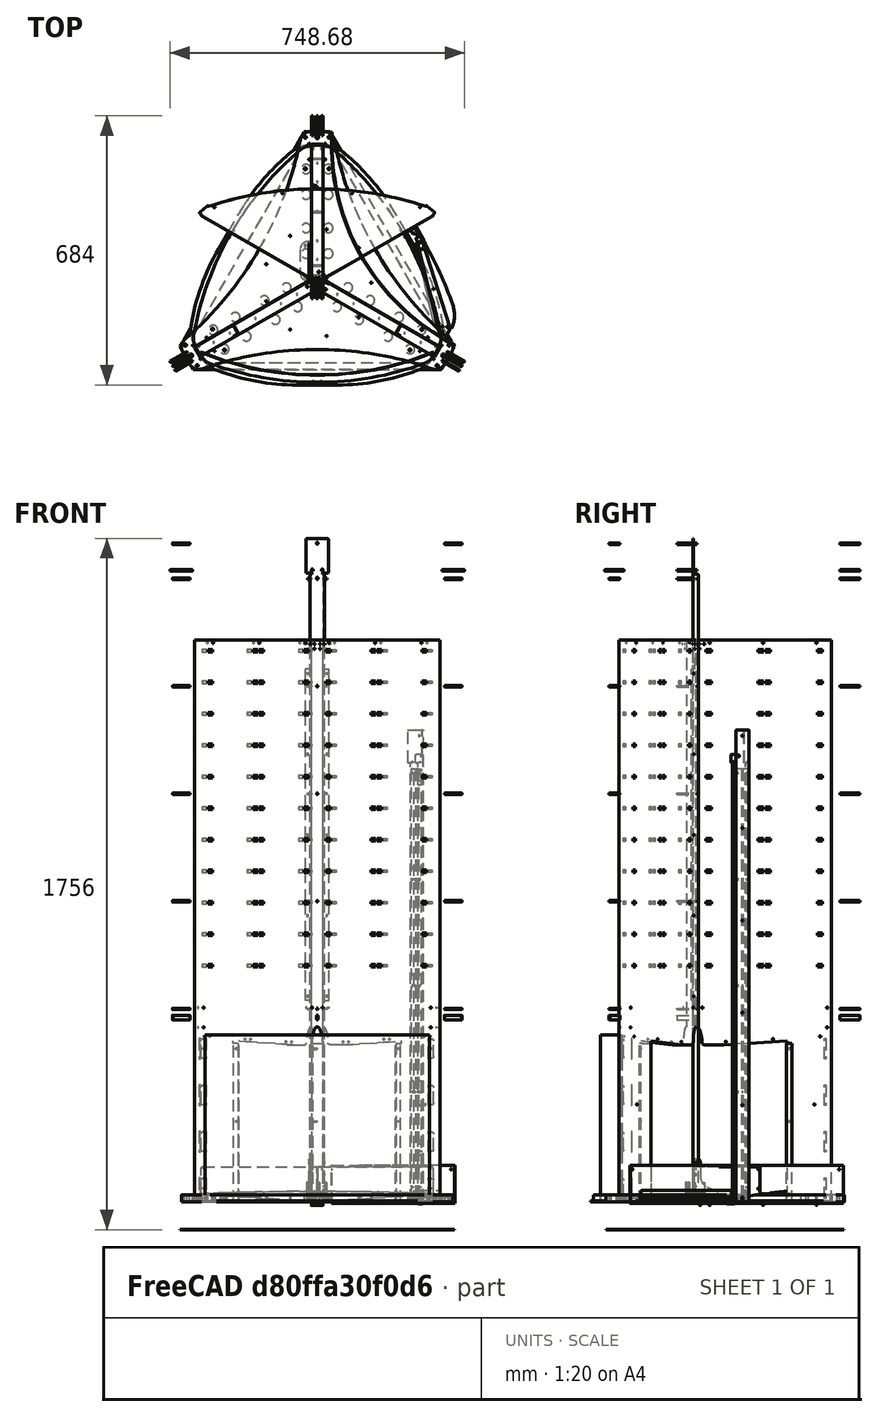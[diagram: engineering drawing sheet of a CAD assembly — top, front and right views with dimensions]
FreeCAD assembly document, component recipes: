
FREECAD ASSEMBLY — COMPONENT RECIPES ("composit_full_size3_door")

This assembly document has 79 components, labeled P0..P78 below (a component is one placed body or linked part). 75 of them carry a construction recipe — the FreeCAD feature program that regenerates the part from scratch, quoted from this document or its linked companion documents; the rest are supplied as boundary geometry only. No exploded tour is included for this assembly.
NOTE — this tour is split across 3 documents so each fits a 32k-token context. This is document 1: the component sections continue in the remaining 2 documents, each repeating the header above.
COMPONENT P0 — recipe-attached ("tech_sector_pillar_material_0.30ansi", modeled in this document).
Construction recipe (the document's own serialized feature program — sketch geometry with constraints, then the solid features built on it; lengths are millimeters unless a unit is written):

FEATURE [Sketcher::SketchObject] Sketch062
  AttachmentSupport = -> [XY_Plane036]
  FullyConstrained = true
  MapMode = 5
  expr: Constraints[3] = <<Properties>>.endface_width / 2 + 0.5 mm
  sketch-geometry (7):
    g0: LineSegment StartX=61.9452 StartY=297.209 StartZ=0 EndX=15 EndY=280 EndZ=0
    g1: LineSegment StartX=15 StartY=280 StartZ=0 EndX=15 EndY=335 EndZ=0
    g2: LineSegment StartX=15 StartY=335 StartZ=0 EndX=62.031 EndY=297.743 EndZ=0
    g3: LineSegment StartX=61.9452 StartY=297.209 StartZ=0 EndX=62.4647 EndY=297.399 EndZ=0
    g4: LineSegment StartX=62.4647 StartY=297.399 StartZ=0 EndX=62.031 EndY=297.743 EndZ=0
    g5: LineSegment StartX=61.9452 StartY=297.209 StartZ=0 EndX=61.8385 EndY=297.5 EndZ=0
    g6: LineSegment StartX=61.8385 StartY=297.5 StartZ=0 EndX=62.031 EndY=297.743 EndZ=0
  constraints (20):
    c: Coincident(g0,g1)
    c: Vertical(g1)
    c: Coincident(g1,g2)
    c: DistanceX(g1) = 15
    c: Distance(g1) = 55
    c: Distance(g2) = 60
    c: Distance(g0) = 50
    c: Coincident(g3,g0)
    c: Coincident(g4,g3)
    c: Coincident(g4,g2)
    c: Parallel(g0,g3)
    c: Parallel(g4,g2)
    c: Equal(g3,g4)
    c: Coincident(g0,g5)
    c: Coincident(g5,g6)
    c: Coincident(g6,g2)
    c: Perpendicular(g3,g5)
    c: Perpendicular(g4,g6)
    c: Distance(g5) = 0.31
    c: DistanceY(g1) = 335
FEATURE [PartDesign::FeaturePython] BaseBend020  # WARN: FeaturePython — macro-defined, semantics opaque (R4)
  BendSide = 0
  BendSketch = -> Sketch062
  MidPlane = false
  Reverse = false
  Suppressed = false
  length = 413
  radius = 0.1
  thickness = 0.3
  expr: radius = composit_properties#<<Properties>>.bend_r
  expr: thickness = composit_properties#<<Properties>>.al_thickness
FEATURE [PartDesign::FeaturePython] Bend009  # WARN: FeaturePython — macro-defined, semantics opaque (R4)
  AutoMiter = true
  BaseFeature = -> BaseBend020
  BendType = 0
  LengthList = [15]
  LengthSpec = 0
  ReliefFactor = 0.7
  Suppressed = false
  UseReliefFactor = false
  angle = 90
  baseObject = -> BaseBend020 [Edge17,Edge4,Edge33,Edge32,Edge16,Edge3]
  bendAList = [90]
  extend1 = 0
  extend2 = 0
  gap1 = 0
  gap2 = 0
  invert = false
  kfactor = 0.5
  length = 15
  maxExtendDist = 5
  minGap = 0.1
  minReliefGap = 1
  miterangle1 = 0
  miterangle2 = 0
  offset = 0
  radius = 0.1
  reliefType = 0
  reliefd = 1
  reliefw = 0.8
  sketchflip = false
  sketchinvert = false
  unfold = false
  expr: radius = BaseBend020.radius
FEATURE [Sketcher::SketchObject] Sketch075
  AttachmentSupport = -> [XY_Plane036]
  ExternalGeometry = -> [Sketch062]
  FullyConstrained = true
  MapMode = 5
  expr: Constraints[34] = <<Properties>>.rivet_d
  sketch-geometry (14):
    g0: LineSegment StartX=15 StartY=280 StartZ=0 EndX=62.4647 EndY=297.399 EndZ=0
    g1: LineSegment StartX=62.4647 StartY=297.399 StartZ=0 EndX=15 EndY=335 EndZ=0
    g2: LineSegment StartX=15 StartY=280 StartZ=0 EndX=30.7162 EndY=302.5 EndZ=0
    g3: LineSegment StartX=30.7162 StartY=302.5 StartZ=0 EndX=15 EndY=335 EndZ=0
    g4: LineSegment StartX=30.7162 StartY=302.5 StartZ=0 EndX=62.4647 EndY=297.399 EndZ=0
    g5: LineSegment StartX=15 StartY=302.5 StartZ=0 EndX=30.7162 EndY=302.5 EndZ=0
    g6: LineSegment StartX=30.7162 StartY=302.5 StartZ=0 EndX=36.1253 EndY=287.744 EndZ=0
    g7: LineSegment StartX=30.7162 StartY=302.5 StartZ=0 EndX=40.4751 EndY=314.819 EndZ=0
    g8: Circle CenterX=34.4044 CenterY=292.439 CenterZ=0 NormalX=0 NormalY=0 NormalZ=1 AngleXU=0 Radius=1.7
    g9: Circle CenterX=36.2097 CenterY=309.435 CenterZ=0 NormalX=0 NormalY=0 NormalZ=1 AngleXU=0 Radius=1.7
    g10: Circle CenterX=20.588 CenterY=302.5 CenterZ=0 NormalX=0 NormalY=0 NormalZ=1 AngleXU=0 Radius=1.7
    g11: LineSegment StartX=20.588 StartY=302.5 StartZ=0 EndX=36.2097 EndY=309.435 EndZ=0
    g12: LineSegment StartX=36.2097 StartY=309.435 StartZ=0 EndX=34.4044 EndY=292.439 EndZ=0
    g13: LineSegment StartX=34.4044 StartY=292.439 StartZ=0 EndX=20.588 EndY=302.5 EndZ=0
  constraints (36):
    c: Coincident(g-4,g0)
    c: Coincident(g0,g1)
    c: Coincident(g1,g-3)
    c: PointOnObject(g-4,g0)
    c: PointOnObject(g-3,g1)
    c: Coincident(g0,g2)
    c: Coincident(g2,g3)
    c: Coincident(g2,g4)
    c: Coincident(g4,g0)
    c: Coincident(g3,g1)
    c: Coincident(g5,g2)
    c: Horizontal(g5)
    c: Coincident(g5,g6)
    c: PointOnObject(g6,g0)
    c: Perpendicular(g0,g6)
    c: Vertical(g5,g0)
    c: Equal(g6,g5)
    c: Coincident(g7,g2)
    c: PointOnObject(g7,g1)
    c: Perpendicular(g1,g7)
    c: Equal(g6,g7)
    c: PointOnObject(g8,g6)
    c: PointOnObject(g9,g7)
    c: PointOnObject(g10,g5)
    c: Coincident(g11,g10)
    c: Coincident(g11,g9)
    c: Coincident(g11,g12)
    c: Coincident(g12,g8)
    c: Coincident(g12,g13)
    c: Coincident(g13,g11)
    c: Equal(g13,g11)
    c: Equal(g11,g12)
    c: Equal(g8,g10)
    c: Equal(g8,g9)
    c: Diameter(g8) = 3.4
    c: Distance(g8,g6) = 5
FEATURE [PartDesign::Pocket] Pocket035
  BaseFeature = -> Bend009
  Direction = (0,0,-1)
  Length = 5
  Length2 = 5
  Midplane = true
  Profile = -> Sketch075
  ReferenceAxis = -> Sketch075 [N_Axis]
  Suppressed = false
  Type = 1
FEATURE [PartDesign::Plane] DatumPlane001
  AttachmentOffset = pos=(0,0,0) rot=(0,1,0;1.5708rad)
  AttachmentSupport = -> [Sketch062]
  Length = 411.982
  MapMode = 7
  Placement = pos=(15,335,0) rot=(-0.89718,0.312304,0.312304;4.6041rad)
  ResizeMode = 0
  Width = 515.08
FEATURE [Sketcher::SketchObject] Sketch077
  AttachmentSupport = -> [DatumPlane001]
  FullyConstrained = true
  MapMode = 5
  Placement = pos=(15,335,0) rot=(0.89718,-0.312304,-0.312304;1.67908rad)
  expr: Constraints[1] = <<Properties>>.rivet_d
  expr: Constraints[3] = BaseBend020.length
  sketch-geometry (4):
    g0: Circle CenterX=10 CenterY=7 CenterZ=0 NormalX=0 NormalY=0 NormalZ=1 AngleXU=0 Radius=1.7
    g1: Circle CenterX=10 CenterY=406 CenterZ=0 NormalX=0 NormalY=0 NormalZ=1 AngleXU=0 Radius=1.7
    g2: GeomPoint X=0 Y=413 Z=0
    g3: LineSegment StartX=0 StartY=206.5 StartZ=0 EndX=10 EndY=206.5 EndZ=0
  constraints (10):
    c: Equal(g0,g1)
    c: Diameter(g0) = 3.4
    c: PointOnObject(g2,g-2)
    c: DistanceY(g2) = 413
    c: DistanceX(g0) = 10
    c: DistanceY(g0) = 7
    c: Vertical(g1,g0)
    c: Horizontal(g3)
    c: Symmetric(g-1,g2,g3)
    c: Symmetric(g1,g0,g3)
FEATURE [PartDesign::Hole] Hole006
  BaseFeature = -> Pocket035
  CustomThreadClearance = 0
  Depth = 1
  DepthType = 0
  Diameter = 3.4
  DrillForDepth = false
  DrillPoint = 1
  DrillPointAngle = 118
  HoleCutCountersinkAngle = 90
  HoleCutCustomValues = false
  HoleCutDepth = 0
  HoleCutDiameter = 6.1
  HoleCutType = 0
  ModelThread = false
  Profile = -> Sketch077
  Reversed = true
  Suppressed = false
  Tapered = false
  TaperedAngle = 90
  ThreadClass = 0
  ThreadDepth = 1
  ThreadDepthType = 0
  ThreadDirection = 0
  ThreadFit = 0
  ThreadSize = 0
  ThreadType = 0
  Threaded = false
  UseCustomThreadClearance = false
  expr: Diameter = <<Properties>>.rivet_d
FEATURE [Sketcher::SketchObject] Sketch078  label="pillar_magnet_fix"
  AttachmentOffset = pos=(0,0,0) rot=(0,1,0;1.5708rad)
  AttachmentSupport = -> [Sketch062]
  FullyConstrained = true
  MapMode = 7
  Placement = pos=(15,280,0) rot=(0.57735,0.57735,0.57735;2.0944rad)
  expr: Constraints[11] = <<Properties>>.rivet_d
  sketch-geometry (8):
    g0: ArcOfCircle CenterX=32.5 CenterY=244.5 CenterZ=0 NormalX=0 NormalY=0 NormalZ=1 AngleXU=0 Radius=11 StartAngle=4.71239 EndAngle=7.85398
    g1: ArcOfCircle CenterX=27.5 CenterY=244.5 CenterZ=0 NormalX=0 NormalY=0 NormalZ=1 AngleXU=0 Radius=11 StartAngle=1.5708 EndAngle=4.71239
    g2: LineSegment StartX=32.5 StartY=255.5 StartZ=0 EndX=27.5 EndY=255.5 EndZ=0
    g3: LineSegment StartX=27.5 StartY=233.5 StartZ=0 EndX=32.5 EndY=233.5 EndZ=0
    g4: Circle CenterX=30 CenterY=224.5 CenterZ=0 NormalX=0 NormalY=0 NormalZ=1 AngleXU=0 Radius=1.7
    g5: Circle CenterX=30 CenterY=264.5 CenterZ=0 NormalX=0 NormalY=0 NormalZ=1 AngleXU=0 Radius=1.7
    g6: LineSegment StartX=27.5 StartY=244.5 StartZ=0 EndX=30 EndY=244.5 EndZ=0
    g7: LineSegment StartX=32.5 StartY=244.5 StartZ=0 EndX=30 EndY=244.5 EndZ=0
  constraints (20):
    c: Tangent(g0,g2) = -1.5708
    c: Tangent(g2,g1) = -1.5708
    c: Tangent(g1,g3) = -1.5708
    c: Tangent(g3,g0) = -1.5708
    c: Equal(g0,g1)
    c: Coincident(g6,g1)
    c: Coincident(g7,g0)
    c: Coincident(g7,g6)
    c: Equal(g6,g7)
    c: Symmetric(g4,g5,g6)
    c: Equal(g4,g5)
    c: Diameter(g4) = 3.4
    c: Parallel(g6,g7)
    c: Distance(g1,g0) = 5
    c: Diameter(g0) = 22
    c: Horizontal(g1,g0)
    c: DistanceY(g4,g5) = 40
    c: DistanceY(g6) = 244.5  'height'
    c: DistanceX(g6) = 30
    c: Vertical(g4,g5)
FEATURE [PartDesign::Pocket] Pocket037
  BaseFeature = -> Hole006
  Direction = (-1,2e-16,0)
  Length = 5
  Length2 = 5
  Midplane = true
  Profile = -> Sketch078
  ReferenceAxis = -> Sketch078 [N_Axis]
  Suppressed = false
  Type = 0
FEATURE [Sketcher::SketchObject] Sketch079
  AttachmentSupport = -> [DatumPlane001]
  FullyConstrained = true
  MapMode = 5
  Placement = pos=(15,335,0) rot=(0.89718,-0.312304,-0.312304;1.67908rad)
  expr: Constraints[3] = BaseBend020.length - 111.35 mm
  sketch-geometry (2):
    g0: Circle CenterX=35 CenterY=301.65 CenterZ=0 NormalX=0 NormalY=0 NormalZ=1 AngleXU=0 Radius=1.25
    g1: Circle CenterX=35 CenterY=205.65 CenterZ=0 NormalX=0 NormalY=0 NormalZ=1 AngleXU=0 Radius=1.25
  constraints (6):
    c: Vertical(g1,g0)
    c: DistanceY(g1,g0) = 96
    c: DistanceX(g1) = 35
    c: DistanceY(g0) = 301.65
    c: Equal(g1,g0)
    c: Diameter(g1) = 2.5
FEATURE [PartDesign::Hole] Hole009
  BaseFeature = -> Pocket037
  CustomThreadClearance = 0
  Depth = 25
  DepthType = 0
  Diameter = 2.5
  DrillForDepth = false
  DrillPoint = 1
  DrillPointAngle = 118
  HoleCutCountersinkAngle = 90
  HoleCutCustomValues = false
  HoleCutDepth = 0
  HoleCutDiameter = 6.1
  HoleCutType = 0
  ModelThread = false
  Profile = -> Sketch079
  Reversed = true
  Suppressed = false
  Tapered = false
  TaperedAngle = 90
  ThreadClass = 0
  ThreadDepth = 25
  ThreadDepthType = 0
  ThreadDirection = 0
  ThreadFit = 0
  ThreadSize = 0
  ThreadType = 0
  Threaded = false
  UseCustomThreadClearance = false
FEATURE [PartDesign::Body] Body073  label="tech_sector_pillar_material_0.30ansi"
  Group = -> [Sketch062,BaseBend020,Bend009,Sketch075,Pocket035,DatumPlane001,Sketch077,Hole006,Sketch078,Pocket037,Sketch079,Hole009]
  Origin = -> Origin036
  Placement = pos=(0,0,3) rot=(0,0,1;0rad)
  Tip = -> Hole009
COMPONENT P1 — recipe-attached ("tech_sector_hor", modeled in this document).
Construction recipe (the document's own serialized feature program — sketch geometry with constraints, then the solid features built on it; lengths are millimeters unless a unit is written):

FEATURE [PartDesign::SubShapeBinder] Binder038
  BindCopyOnChange = 0
  BindMode = 0
  ClaimChildren = true
  Context = -> Body074 [Binder038.]
  Fuse = false
  MakeFace = true
  OffsetFill = false
  OffsetIntersection = false
  OffsetJoinType = 0
  OffsetOpenResult = false
  PartialLoad = false
  Relative = true
  Support = -> [Compound037]
  _Version = 2
FEATURE [PartDesign::Pad] Pad008
  Direction = (0,0,1)
  Length = 3
  Length2 = 10
  Profile = -> Binder038
  Suppressed = false
  Type = 0
FEATURE [PartDesign::SubShapeBinder] Binder044
  BindCopyOnChange = 0
  BindMode = 0
  ClaimChildren = false
  Context = -> Body074 [Binder044.]
  Fuse = false
  MakeFace = true
  OffsetFill = false
  OffsetIntersection = false
  OffsetJoinType = 0
  OffsetOpenResult = false
  PartialLoad = false
  Relative = true
  Support = -> [Body073[Pocket035.Sketch075.]]
  _Version = 2
FEATURE [PartDesign::Pocket] Pocket036
  BaseFeature = -> Pad008
  Direction = (0,0,-1)
  Length = 5
  Length2 = 5
  Midplane = true
  Profile = -> Binder044
  Suppressed = false
  Type = 1
FEATURE [PartDesign::Plane] DatumPlane
  AttachmentOffset = pos=(0,0,0) rot=(0,1,0;0.523599rad)
  AttachmentSupport = -> [XZ_Plane037]
  Length = 552.693
  MapMode = 5
  Placement = pos=(0,0,0) rot=(0.935113,0.250563,0.250563;1.63783rad)
  ResizeMode = 0
  Width = 82.2624
FEATURE [PartDesign::Mirrored] Mirrored003
  BaseFeature = -> Pocket036
  MirrorPlane = -> DatumPlane
  Originals = -> [Pocket036]
  Suppressed = false
FEATURE [Sketcher::SketchObject] Sketch083
  AttachmentSupport = -> [XY_Plane037]
  ExternalGeometry = -> [Binder038]
  FullyConstrained = true
  MapMode = 5
  expr: Constraints[4] = <<Properties>>.rivet_d
  sketch-geometry (2):
    g0: LineSegment StartX=212.95 StartY=122.947 StartZ=0 EndX=201.691 EndY=116.447 EndZ=0
    g1: Circle CenterX=201.691 CenterY=116.447 CenterZ=0 NormalX=0 NormalY=0 NormalZ=1 AngleXU=0 Radius=1.7
  constraints (5):
    c: Coincident(g0,g-3)
    c: Perpendicular(g-3,g0)
    c: Distance(g0) = 13
    c: Coincident(g1,g0)
    c: Diameter(g1) = 3.4
FEATURE [PartDesign::Hole] Hole011
  BaseFeature = -> Mirrored003
  CustomThreadClearance = 0
  Depth = 25
  DepthType = 0
  Diameter = 3.4
  DrillForDepth = false
  DrillPoint = 1
  DrillPointAngle = 118
  HoleCutCountersinkAngle = 90
  HoleCutCustomValues = false
  HoleCutDepth = 0
  HoleCutDiameter = 6.1
  HoleCutType = 0
  ModelThread = false
  Profile = -> Sketch083
  Reversed = true
  Suppressed = false
  Tapered = false
  TaperedAngle = 90
  ThreadClass = 0
  ThreadDepth = 25
  ThreadDepthType = 0
  ThreadDirection = 0
  ThreadFit = 0
  ThreadSize = 0
  ThreadType = 0
  Threaded = false
  UseCustomThreadClearance = false
  expr: Diameter = <<Properties>>.rivet_d
FEATURE [PartDesign::Body] Body074  label="tech_sector_hor"
  Group = -> [Binder038,Pad008,Binder044,Pocket036,DatumPlane,Mirrored003,Sketch083,Hole011]
  Origin = -> Origin037
  Tip = -> Hole011
COMPONENT P2 — recipe-attached ("tech_sector_plexiglass_material_0.30ansi", modeled in this document).
Construction recipe (the document's own serialized feature program — sketch geometry with constraints, then the solid features built on it; lengths are millimeters unless a unit is written):

FEATURE [PartDesign::SubShapeBinder] Binder045
  BindCopyOnChange = 0
  BindMode = 0
  ClaimChildren = false
  Context = -> Body077 [Binder045.]
  Fuse = false
  MakeFace = true
  OffsetFill = false
  OffsetIntersection = false
  OffsetJoinType = 0
  OffsetOpenResult = false
  PartialLoad = false
  Relative = true
  Support = -> [Body074[Binder038.Compound037.Sketch063.]]
  _Version = 2
FEATURE [Sketcher::SketchObject] Sketch076
  AttachmentSupport = -> [XY_Plane041]
  ExternalGeometry = -> [Binder045]
  FullyConstrained = true
  MapMode = 5
  sketch-geometry (5):
    g0: LineSegment StartX=15 StartY=335 StartZ=0 EndX=62.031 EndY=297.743 EndZ=0
    g1: ArcOfCircle CenterX=-320.353 CenterY=-184.956 CenterZ=0 NormalX=0 NormalY=0 NormalZ=1 AngleXU=0 Radius=615.805 StartAngle=0.146355 EndAngle=0.900842
    g2: LineSegment StartX=288.868 StartY=-95.1511 StartZ=0 EndX=297.619 EndY=-154.51 EndZ=0
    g3: LineSegment StartX=-320.353 StartY=-184.956 StartZ=0 EndX=212.95 EndY=122.947 EndZ=0
    g4: LineSegment StartX=62.031 StartY=297.743 StartZ=0 EndX=288.868 EndY=-95.1511 EndZ=0
  constraints (12):
    c: Coincident(g0,g-4)
    c: Coincident(g1,g-4)
    c: Coincident(g1,g0)
    c: Tangent(g2,g1) = 1.5708
    c: Coincident(g3,g1)
    c: Coincident(g3,g-4)
    c: Vertical(g0,g-5)
    c: Equal(g0,g2)
    c: PointOnObject(g-3,g0)
    c: Coincident(g4,g0)
    c: Coincident(g4,g1)
    c: Perpendicular(g3,g4)
FEATURE [PartDesign::FeaturePython] BaseBend021  # WARN: FeaturePython — macro-defined, semantics opaque (R4)
  BendSide = 1
  BendSketch = -> Sketch076
  MidPlane = false
  Reverse = false
  Suppressed = false
  length = 419
  radius = 1
  thickness = 1.5
  expr: length = BaseBend020.length + composit_properties#<<Properties>>.thickness * 2
FEATURE [PartDesign::Fillet] Fillet
  Base = -> BaseBend021 [Edge10,Edge8,Edge25,Edge23]
  BaseFeature = -> BaseBend021
  Radius = 3
  SupportTransform = false
  Suppressed = false
  UseAllEdges = false
FEATURE [PartDesign::SubShapeBinder] Binder046
  BindCopyOnChange = 0
  BindMode = 0
  ClaimChildren = false
  Context = -> Body077 [Binder046.]
  Fuse = false
  MakeFace = true
  OffsetFill = false
  OffsetIntersection = false
  OffsetJoinType = 0
  OffsetOpenResult = false
  PartialLoad = false
  Relative = true
  Support = -> [Body073[Hole006.Sketch077.]]
  _Version = 2
FEATURE [PartDesign::SubShapeBinder] Binder047
  BindCopyOnChange = 0
  BindMode = 0
  ClaimChildren = true
  Context = -> Body077 [Binder047.]
  Fuse = false
  MakeFace = true
  OffsetFill = false
  OffsetIntersection = false
  OffsetJoinType = 0
  OffsetOpenResult = false
  PartialLoad = false
  Relative = true
  Support = -> [Body073[Sketch079.]]
  _Version = 2
FEATURE [PartDesign::Plane] DatumPlane002
  AttachmentOffset = pos=(0,0,0) rot=(0,1,0;0.523599rad)
  AttachmentSupport = -> [XZ_Plane041]
  Length = 622.679
  MapMode = 5
  Placement = pos=(0,0,0) rot=(0.935113,0.250563,0.250563;1.63783rad)
  ResizeMode = 0
  Width = 540.655
FEATURE [Sketcher::SketchObject] Sketch084
  AttachmentSupport = -> [Binder046]
  ExternalGeometry = -> [Binder046]
  FullyConstrained = false
  MapMode = 5
  Placement = pos=(168.839,213.132,5.44e-14) rot=(0.239007,0.686613,0.686613;2.67238rad)
  sketch-geometry (3):
    g0: Circle CenterX=186.261 CenterY=10.25 CenterZ=0 NormalX=0 NormalY=0 NormalZ=1 AngleXU=0 Radius=1.69397
    g1: Circle CenterX=186.261 CenterY=408.75 CenterZ=0 NormalX=0 NormalY=0 NormalZ=1 AngleXU=0 Radius=1.72481
    g2: GeomPoint X=186.261 Y=209.5 Z=0
  constraints (4):
    c: Symmetric(g-4,g-3,g2)
    c: Symmetric(g1,g0,g2)
    c: Vertical(g-3,g0)
    c: DistanceY(g-3,g0) = 0.25
FEATURE [PartDesign::Hole] Hole007
  BaseFeature = -> Fillet
  CustomThreadClearance = 0
  Depth = 25
  DepthType = 0
  Diameter = 3.4
  DrillForDepth = false
  DrillPoint = 1
  DrillPointAngle = 118
  HoleCutCountersinkAngle = 90
  HoleCutCustomValues = false
  HoleCutDepth = 0
  HoleCutDiameter = 6.1
  HoleCutType = 0
  ModelThread = false
  Profile = -> Sketch084
  Reversed = true
  Suppressed = false
  Tapered = false
  TaperedAngle = 90
  ThreadClass = 0
  ThreadDepth = 25
  ThreadDepthType = 0
  ThreadDirection = 0
  ThreadFit = 0
  ThreadSize = 0
  ThreadType = 0
  Threaded = false
  UseCustomThreadClearance = false
  expr: Diameter = <<Properties>>.rivet_d
FEATURE [PartDesign::Hole] Hole008
  BaseFeature = -> Hole007
  CustomThreadClearance = 0
  Depth = 25
  DepthType = 0
  Diameter = 3.4
  DrillForDepth = false
  DrillPoint = 1
  DrillPointAngle = 118
  HoleCutCountersinkAngle = 90
  HoleCutCustomValues = false
  HoleCutDepth = 0
  HoleCutDiameter = 6.1
  HoleCutType = 0
  ModelThread = false
  Profile = -> Binder047
  Reversed = true
  Suppressed = false
  Tapered = false
  TaperedAngle = 90
  ThreadClass = 0
  ThreadDepth = 25
  ThreadDepthType = 0
  ThreadDirection = 0
  ThreadFit = 0
  ThreadSize = 0
  ThreadType = 0
  Threaded = false
  UseCustomThreadClearance = false
  expr: Diameter = <<Properties>>.rivet_d
FEATURE [PartDesign::Mirrored] Mirrored004
  BaseFeature = -> Hole008
  MirrorPlane = -> DatumPlane002
  Originals = -> [Hole007,Hole008]
  Suppressed = false
FEATURE [PartDesign::Body] Body077  label="tech_sector_plexiglass_material_0.30ansi"
  Group = -> [Binder045,Sketch076,BaseBend021,Fillet,Binder046,Hole007,Binder047,Hole008,DatumPlane002,Mirrored004,Sketch084]
  Origin = -> Origin041
  Tip = -> Mirrored004
COMPONENT P3 — recipe-attached ("basement_amplifier_material_0.30ansi", modeled in this document).
Construction recipe (the document's own serialized feature program — sketch geometry with constraints, then the solid features built on it; lengths are millimeters unless a unit is written):

FEATURE [Sketcher::SketchObject] Sketch121
  AttachmentSupport = -> [XZ_Plane054]
  FullyConstrained = true
  MapMode = 5
  Placement = pos=(0,0,0) rot=(1,0,0;1.5708rad)
  sketch-geometry (5):
    g0: LineSegment StartX=-18 StartY=15 StartZ=0 EndX=-18 EndY=0 EndZ=0
    g1: LineSegment StartX=-18 StartY=0 StartZ=0 EndX=18 EndY=0 EndZ=0
    g2: LineSegment StartX=18 StartY=0 StartZ=0 EndX=18 EndY=15 EndZ=0
    g3: LineSegment StartX=18 StartY=15 StartZ=0 EndX=-18 EndY=15 EndZ=0
    g4: GeomPoint X=0 Y=7.5 Z=0
  constraints (13):
    c: Coincident(g0,g1)
    c: Coincident(g1,g2)
    c: Coincident(g2,g3)
    c: Coincident(g3,g0)
    c: Horizontal(g1)
    c: Horizontal(g3)
    c: Vertical(g0)
    c: Vertical(g2)
    c: Symmetric(g1,g0,g4)
    c: PointOnObject(g4,g-2)
    c: PointOnObject(g1,g-1)
    c: DistanceY(g2,g2) = 15  'height'
    c: DistanceX(g1,g1) = 36  'width'
FEATURE [PartDesign::FeaturePython] BaseBend030  # WARN: FeaturePython — macro-defined, semantics opaque (R4)
  BendSide = 1
  BendSketch = -> Sketch121
  MidPlane = true
  Reverse = false
  Suppressed = false
  length = 245
  radius = 2
  thickness = 2
FEATURE [Sketcher::SketchObject] Sketch122
  AttachmentSupport = -> [YZ_Plane054]
  FullyConstrained = true
  MapMode = 5
  Placement = pos=(0,0,0) rot=(0.57735,0.57735,0.57735;2.0944rad)
  expr: Constraints[10] = Sketch121.Constraints.height
  expr: Constraints[12] = BaseBend030.length / 2
  expr: Constraints[9] = BaseBend030.thickness + BaseBend030.radius
  sketch-geometry (14):
    g0: ArcOfCircle CenterX=117.5 CenterY=4 CenterZ=0 NormalX=0 NormalY=0 NormalZ=1 AngleXU=0 Radius=5 StartAngle=1e-16 EndAngle=0.785398
    g1: LineSegment StartX=121.036 StartY=7.53553 StartZ=0 EndX=115.036 EndY=13.5355 EndZ=0
    g2: ArcOfCircle CenterX=111.5 CenterY=10 CenterZ=0 NormalX=0 NormalY=0 NormalZ=1 AngleXU=0 Radius=5 StartAngle=0.785398 EndAngle=1.5708
    g3: LineSegment StartX=111.5 StartY=15 StartZ=0 EndX=-111.5 EndY=15 EndZ=0
    g4: LineSegment StartX=122.5 StartY=4 StartZ=0 EndX=122.5 EndY=0 EndZ=0
    g5: LineSegment StartX=122.5 StartY=0 StartZ=0 EndX=-122.5 EndY=0 EndZ=0
    g6: LineSegment StartX=-122.5 StartY=0 StartZ=0 EndX=-122.5 EndY=4 EndZ=0
    g7: LineSegment StartX=-121.036 StartY=7.53553 StartZ=0 EndX=-115.036 EndY=13.5355 EndZ=0
    g8: ArcOfCircle CenterX=-111.5 CenterY=10 CenterZ=0 NormalX=0 NormalY=0 NormalZ=1 AngleXU=0 Radius=5 StartAngle=1.5708 EndAngle=2.35619
    g9: GeomPoint X=-113.571 Y=15 Z=0
    g10: ArcOfCircle CenterX=-117.5 CenterY=4 CenterZ=0 NormalX=0 NormalY=0 NormalZ=1 AngleXU=0 Radius=5 StartAngle=2.35619 EndAngle=3.14159
    g11: GeomPoint X=-122.5 Y=6.07107 Z=0
    g12: GeomPoint X=113.571 Y=15 Z=0
    g13: GeomPoint X=122.5 Y=6.07107 Z=0
  constraints (32):
    c: Tangent(g1,g0) = -1.5708
    c: Angle(g1) = 2.35619
    c: Tangent(g2,g1) = -1.5708
    c: Horizontal(g3)
    c: Tangent(g3,g2) = -1.5708
    c: Equal(g0,g2)
    c: Tangent(g0,g4) = 1.5708
    c: Coincident(g4,g5)
    c: Horizontal(g5)
    c: DistanceY(g0) = 4
    c: DistanceY(g9) = 15
    c: Vertical(g4)
    c: DistanceX(g4) = 122.5
    c: Radius(g0) = 5
    c: Coincident(g5,g6)
    c: Tangent(g3,g8) = -1.5708
    c: Tangent(g7,g8) = 1.5708
    c: PointOnObject(g11,g6)
    c: PointOnObject(g11,g7)
    c: Tangent(g6,g10) = 1.5708
    c: Tangent(g7,g10) = 1.5708
    c: Vertical(g6)
    c: Equal(g10,g8)
    c: Equal(g8,g2)
    c: PointOnObject(g13,g4)
    c: PointOnObject(g13,g1)
    c: PointOnObject(g12,g1)
    c: Symmetric(g13,g11,g-2)
    c: Symmetric(g9,g12,g-2)
    c: PointOnObject(g9,g3)
    c: PointOnObject(g9,g7)
    c: PointOnObject(g-1,g5)
FEATURE [Part::FeaturePython] WireFilter003  # WARN: FeaturePython — macro-defined, semantics opaque (R4)
  AttacherType = Attacher::AttachEngine3D
  ClaimChildren = true
  ColorKeyCount = 8
  Colorize = true
  FaceMaker = 5
  FixNormal = false
  FollowSource = true
  InvertedFaceScale = 5
  MaxWires = 25
  Normal = (1,-3e-16,2e-16)
  OffsetFill = false
  OffsetIntersection = false
  OffsetJoin = 0
  OffsetOpenResult = false
  Scale = (1,1,1)
  SelectEdges = false
  Source = -> Sketch122
  UniformScale = 1
  UseDefault = false
  UseSelected = true
  UseSelectedEdges = false
  Version = 0.2022.02.09
  WireOrder = [1]
FEATURE [PartDesign::Pocket] Pocket066
  BaseFeature = -> BaseBend030
  Direction = (-1,3e-16,-2e-16)
  Length = 5
  Length2 = 5
  Midplane = true
  Profile = -> WireFilter003
  Suppressed = false
  Type = 1
FEATURE [Sketcher::SketchObject] Sketch123
  AttachmentSupport = -> [XY_Plane054]
  FullyConstrained = true
  MapMode = 5
  expr: Constraints[1] = -BaseBend030.length / 2
  expr: Constraints[32] = BaseBend030.length - 14 mm
  sketch-geometry (15):
    g0: GeomPoint X=0 Y=-122.5 Z=0
    g1: Circle CenterX=0 CenterY=92.5 CenterZ=0 NormalX=0 NormalY=0 NormalZ=1 AngleXU=0 Radius=2.5
    g2: LineSegment StartX=9 StartY=115.5 StartZ=0 EndX=-9 EndY=115.5 EndZ=0
    g3: LineSegment StartX=-9 StartY=115.5 StartZ=0 EndX=-9 EndY=0 EndZ=0
    g4: LineSegment StartX=-9 StartY=0 StartZ=0 EndX=-9 EndY=-115.5 EndZ=0
    g5: LineSegment StartX=-9 StartY=-115.5 StartZ=0 EndX=9 EndY=-115.5 EndZ=0
    g6: LineSegment StartX=9 StartY=-115.5 StartZ=0 EndX=9 EndY=0 EndZ=0
    g7: LineSegment StartX=9 StartY=0 StartZ=0 EndX=9 EndY=115.5 EndZ=0
    g8: Circle CenterX=-9 CenterY=0 CenterZ=0 NormalX=0 NormalY=0 NormalZ=1 AngleXU=0 Radius=2.5
    g9: Circle CenterX=9 CenterY=0 CenterZ=0 NormalX=0 NormalY=0 NormalZ=1 AngleXU=0 Radius=2.5
    g10: Circle CenterX=-9 CenterY=115.5 CenterZ=0 NormalX=0 NormalY=0 NormalZ=1 AngleXU=0 Radius=2.5
    g11: Circle CenterX=9 CenterY=115.5 CenterZ=0 NormalX=0 NormalY=0 NormalZ=1 AngleXU=0 Radius=2.5
    g12: Circle CenterX=-9 CenterY=-115.5 CenterZ=0 NormalX=0 NormalY=0 NormalZ=1 AngleXU=0 Radius=2.5
    g13: Circle CenterX=9 CenterY=-115.5 CenterZ=0 NormalX=0 NormalY=0 NormalZ=1 AngleXU=0 Radius=2.5
    g14: Circle CenterX=0 CenterY=-92.5 CenterZ=0 NormalX=0 NormalY=0 NormalZ=1 AngleXU=0 Radius=4
  constraints (36):
    c: PointOnObject(g0,g-2)
    c: DistanceY(g0) = -122.5
    c: PointOnObject(g1,g-2)
    c: DistanceY(g0,g1) = 215
    c: Horizontal(g2)
    c: Coincident(g2,g3)
    c: PointOnObject(g3,g-1)
    c: Vertical(g3)
    c: Coincident(g3,g4)
    c: Vertical(g4)
    c: Coincident(g4,g5)
    c: Horizontal(g5)
    c: Coincident(g5,g6)
    c: PointOnObject(g6,g-1)
    c: Vertical(g6)
    c: Coincident(g6,g7)
    c: Coincident(g7,g2)
    c: Vertical(g7)
    c: Coincident(g8,g3)
    c: Coincident(g9,g6)
    c: Coincident(g10,g2)
    c: Coincident(g11,g2)
    c: Coincident(g12,g4)
    c: Coincident(g13,g5)
    c: Symmetric(g12,g11,g-1)
    c: Equal(g11,g10)
    c: Equal(g11,g1)
    c: Equal(g11,g8)
    c: Equal(g11,g9)
    c: Equal(g11,g12)
    c: Equal(g11,g13)
    c: Diameter(g11) = 5
    c: DistanceY(g12,g10) = 231
    c: DistanceX(g2,g2) = 18
    c: Diameter(g14) = 8
    c: Symmetric(g14,g1,g-1)
FEATURE [PartDesign::Pocket] Pocket067
  BaseFeature = -> Pocket066
  Direction = (0,0,-1)
  Length = 5
  Length2 = 5
  Profile = -> Sketch123
  ReferenceAxis = -> Sketch123 [N_Axis]
  Reversed = true
  Suppressed = false
  Type = 0
FEATURE [PartDesign::Body] Body088  label="basement_amplifier_material_0.30ansi"
  Group = -> [Sketch121,BaseBend030,Sketch122,WireFilter003,Pocket066,Sketch123,Pocket067]
  Origin = -> Origin054
  Tip = -> Pocket067
COMPONENT P4 — recipe-attached ("door_base_pillar_material_0.45ansi", modeled in this document).
Construction recipe (the document's own serialized feature program — sketch geometry with constraints, then the solid features built on it; lengths are millimeters unless a unit is written):

FEATURE [PartDesign::SubShapeBinder] Binder083
  BindCopyOnChange = 0
  BindMode = 0
  ClaimChildren = true
  Context = -> Body095 [Binder083.]
  Fuse = false
  MakeFace = true
  OffsetFill = false
  OffsetIntersection = false
  OffsetJoinType = 0
  OffsetOpenResult = false
  PartialLoad = false
  Relative = false
  Support = -> [Sketch128]
  _Version = 2
FEATURE [PartDesign::FeaturePython] BaseBend034  label="door_base_pillar_BaseBend"  # WARN: FeaturePython — macro-defined, semantics opaque (R4)
  BendSide = 0
  BendSketch = -> Binder083
  MidPlane = false
  Reverse = false
  Suppressed = false
  length = 1200
  radius = 2
  thickness = 1
FEATURE [PartDesign::SubShapeBinder] Binder092
  BindCopyOnChange = 0
  BindMode = 0
  ClaimChildren = true
  Context = -> Body095 [Binder092.]
  Fuse = false
  MakeFace = true
  OffsetFill = false
  OffsetIntersection = false
  OffsetJoinType = 0
  OffsetOpenResult = false
  PartialLoad = false
  Relative = true
  Support = -> [Sketch141]
  _Version = 2
FEATURE [PartDesign::Pocket] Pocket075
  BaseFeature = -> BaseBend034
  Direction = (0,-1,2e-16)
  Length = 5
  Length2 = 5
  Midplane = true
  Profile = -> Binder092
  Suppressed = false
  Type = 1
FEATURE [Sketcher::SketchObject] Sketch159
  AttachmentSupport = -> [BaseBend034]
  FullyConstrained = true
  MapMode = 5
  Placement = pos=(40.5,0,0) rot=(0.57735,0.57735,0.57735;2.0944rad)
  sketch-geometry (2):
    g0: Circle CenterX=345 CenterY=1094 CenterZ=0 NormalX=0 NormalY=0 NormalZ=1 AngleXU=0 Radius=1.7
    g1: Circle CenterX=345 CenterY=154 CenterZ=0 NormalX=0 NormalY=0 NormalZ=1 AngleXU=0 Radius=1.7
  constraints (6):
    c: DistanceY(g0) = 1094
    c: DistanceY(g1,g0) = 940
    c: Equal(g0,g1)
    c: Diameter(g0) = 3.4
    c: Vertical(g1,g0)
    c: DistanceX(g0) = 345
FEATURE [Sketcher::SketchObject] Sketch160
  AttachmentSupport = -> [BaseBend034]
  FullyConstrained = true
  MapMode = 5
  Placement = pos=(31.1979,356.594,0) rot=(0.998099,-0.043578,-0.043578;1.5727rad)
  sketch-geometry (8):
    g0: Circle CenterX=17.5 CenterY=1094 CenterZ=0 NormalX=0 NormalY=0 NormalZ=1 AngleXU=0 Radius=1.7
    g1: Circle CenterX=33.5 CenterY=1094 CenterZ=0 NormalX=0 NormalY=0 NormalZ=1 AngleXU=0 Radius=1.7
    g2: Circle CenterX=17.5 CenterY=154 CenterZ=0 NormalX=0 NormalY=0 NormalZ=1 AngleXU=0 Radius=1.7
    g3: Circle CenterX=33.5 CenterY=154 CenterZ=0 NormalX=0 NormalY=0 NormalZ=1 AngleXU=0 Radius=1.7
    g4: LineSegment StartX=17.5 StartY=154 StartZ=0 EndX=33.5 EndY=154 EndZ=0
    g5: LineSegment StartX=33.5 StartY=154 StartZ=0 EndX=33.5 EndY=1094 EndZ=0
    g6: LineSegment StartX=33.5 StartY=1094 StartZ=0 EndX=17.5 EndY=1094 EndZ=0
    g7: LineSegment StartX=17.5 StartY=1094 StartZ=0 EndX=17.5 EndY=154 EndZ=0
  constraints (20):
    c: Equal(g0,g1)
    c: Diameter(g0) = 3.4
    c: Equal(g2,g3)
    c: Equal(g3,g0)
    c: Coincident(g4,g5)
    c: Coincident(g5,g6)
    c: Coincident(g6,g7)
    c: Coincident(g7,g4)
    c: Horizontal(g4)
    c: Horizontal(g6)
    c: Vertical(g5)
    c: Vertical(g7)
    c: Coincident(g4,g2)
    c: Coincident(g5,g1)
    c: Coincident(g4,g3)
    c: Coincident(g6,g0)
    c: DistanceY(g0) = 1094
    c: DistanceY(g7,g7) = 940
    c: DistanceX(g6,g6) = 16
    c: DistanceX(g0) = 17.5
FEATURE [Sketcher::SketchObject] Sketch161
  AttachmentSupport = -> [BaseBend034]
  FullyConstrained = true
  MapMode = 5
  Placement = pos=(40.5,0,0) rot=(0.57735,0.57735,0.57735;2.0944rad)
  sketch-geometry (8):
    g0: Circle CenterX=343.262 CenterY=363.2 CenterZ=0 NormalX=0 NormalY=0 NormalZ=1 AngleXU=0 Radius=2
    g1: Circle CenterX=343.262 CenterY=300 CenterZ=0 NormalX=0 NormalY=0 NormalZ=1 AngleXU=0 Radius=2
    g2: Circle CenterX=343.262 CenterY=1063 CenterZ=0 NormalX=0 NormalY=0 NormalZ=1 AngleXU=0 Radius=2
    g3: Circle CenterX=343.262 CenterY=999.8 CenterZ=0 NormalX=0 NormalY=0 NormalZ=1 AngleXU=0 Radius=2
    g4: LineSegment StartX=343.262 StartY=1063 StartZ=0 EndX=343.262 EndY=999.8 EndZ=0
    g5: LineSegment StartX=343.262 StartY=999.8 StartZ=0 EndX=343.262 EndY=363.2 EndZ=0
    g6: LineSegment StartX=343.262 StartY=363.2 StartZ=0 EndX=343.262 EndY=300 EndZ=0
    g7: GeomPoint X=353.262 Y=301.263 Z=0
  constraints (21):
    c: Coincident(g4,g2)
    c: Vertical(g4)
    c: Coincident(g4,g5)
    c: Coincident(g5,g0)
    c: Vertical(g5)
    c: Coincident(g5,g6)
    c: Coincident(g6,g1)
    c: Vertical(g6)
    c: Coincident(g4,g3)
    c: Equal(g4,g6)
    c: DistanceY(g6,g6) = 63.2
    c: DistanceY(g2) = 1063
    c: DistanceY(g1) = 300
    c: Equal(g1,g0)
    c: Equal(g1,g3)
    c: Equal(g1,g2)
    c: Diameter(g1) = 4
    c: DistanceX(g1) = 343.262
    c: DistanceX(g7) = 353.262
    c: DistanceY(g7) = 301.263
    c: DistanceX(g1,g7) = 10
FEATURE [Sketcher::SketchObject] Sketch162
  AttachmentSupport = -> [BaseBend034]
  FullyConstrained = true
  MapMode = 5
  Placement = pos=(31.1979,356.594,0) rot=(0.998099,-0.043578,-0.043578;1.5727rad)
  sketch-geometry (11):
    g0: LineSegment StartX=20 StartY=15 StartZ=0 EndX=20 EndY=250 EndZ=0
    g1: LineSegment StartX=20 StartY=250 StartZ=0 EndX=20 EndY=485 EndZ=0
    g2: LineSegment StartX=20 StartY=485 StartZ=0 EndX=20 EndY=720 EndZ=0
    g3: LineSegment StartX=20 StartY=720 StartZ=0 EndX=20 EndY=955 EndZ=0
    g4: LineSegment StartX=20 StartY=955 StartZ=0 EndX=20 EndY=1190 EndZ=0
    g5: Circle CenterX=20 CenterY=15 CenterZ=0 NormalX=0 NormalY=0 NormalZ=1 AngleXU=0 Radius=1.7
    g6: Circle CenterX=20 CenterY=250 CenterZ=0 NormalX=0 NormalY=0 NormalZ=1 AngleXU=0 Radius=1.7
    g7: Circle CenterX=20 CenterY=485 CenterZ=0 NormalX=0 NormalY=0 NormalZ=1 AngleXU=0 Radius=1.7
    g8: Circle CenterX=20 CenterY=720 CenterZ=0 NormalX=0 NormalY=0 NormalZ=1 AngleXU=0 Radius=1.7
    g9: Circle CenterX=20 CenterY=955 CenterZ=0 NormalX=0 NormalY=0 NormalZ=1 AngleXU=0 Radius=1.7
    g10: Circle CenterX=20 CenterY=1190 CenterZ=0 NormalX=0 NormalY=0 NormalZ=1 AngleXU=0 Radius=1.7
  constraints (24):
    c: Vertical(g0)
    c: Coincident(g0,g1)
    c: Vertical(g1)
    c: Coincident(g1,g2)
    c: Vertical(g2)
    c: Coincident(g2,g3)
    c: Vertical(g3)
    c: Coincident(g3,g4)
    c: Vertical(g4)
    c: Equal(g0,g1)
    c: Equal(g1,g2)
    c: Equal(g2,g3)
    c: Equal(g3,g4)
    c: Coincident(g5,g0)
    c: Coincident(g6,g0)
    c: Coincident(g7,g1)
    c: Coincident(g8,g2)
    c: Coincident(g9,g3)
    c: Coincident(g10,g4)
    c: Equal(g5, g6-g10) x5
    c: Diameter(g5) = 3.4
    c: DistanceY(g10) = 1190
    c: DistanceY(g5) = 15
    c: DistanceX(g5) = 20
FEATURE [PartDesign::Pocket] Pocket095
  BaseFeature = -> Pocket075
  Direction = (0.0871557,0.996195,3e-16)
  Length = 5
  Length2 = 5
  Profile = -> Sketch162
  ReferenceAxis = -> Sketch162 [N_Axis]
  Suppressed = false
  Type = 0
FEATURE [PartDesign::Pocket] Pocket094
  BaseFeature = -> Pocket095
  Direction = (-1,0,0)
  Length = 5
  Length2 = 5
  Profile = -> Sketch161
  ReferenceAxis = -> Sketch161 [N_Axis]
  Suppressed = false
  Type = 0
FEATURE [PartDesign::Pocket] Pocket090
  BaseFeature = -> Pocket094
  Direction = (-1,0,0)
  Length = 5
  Length2 = 5
  Profile = -> Sketch159
  ReferenceAxis = -> Sketch159 [N_Axis]
  Suppressed = false
  Type = 0
FEATURE [PartDesign::Pocket] Pocket091
  BaseFeature = -> Pocket090
  Direction = (0.0871557,0.996195,3e-16)
  Length = 5
  Length2 = 5
  Profile = -> Sketch160
  ReferenceAxis = -> Sketch160 [N_Axis]
  Suppressed = false
  Type = 0
FEATURE [PartDesign::Body] Body095  label="door_base_pillar_material_0.45ansi"
  Group = -> [Binder083,BaseBend034,Pocket075,Binder092,Sketch159,Sketch160,Sketch161,Sketch162,Pocket095,Pocket094,Pocket090,Pocket091]
  Origin = -> Origin061
  Tip = -> Pocket091
COMPONENT P5 — recipe-attached ("led_holder2", modeled in this document).
Construction recipe (the document's own serialized feature program — sketch geometry with constraints, then the solid features built on it; lengths are millimeters unless a unit is written):

FEATURE [Sketcher::SketchObject] Sketch205
  AttachmentSupport = -> [XZ_Plane096]
  FullyConstrained = true
  MapMode = 5
  Placement = pos=(0,0,0) rot=(1,0,0;1.5708rad)
  sketch-geometry (4):
    g0: LineSegment StartX=0.1 StartY=485 StartZ=0 EndX=-14 EndY=485 EndZ=0
    g1: LineSegment StartX=-14 StartY=485 StartZ=0 EndX=-14 EndY=1590 EndZ=0
    g2: LineSegment StartX=-14 StartY=1590 StartZ=0 EndX=0.1 EndY=1590 EndZ=0
    g3: LineSegment StartX=0.1 StartY=1590 StartZ=0 EndX=0.1 EndY=485 EndZ=0
  constraints (13):
    c: Coincident(g0,g1)
    c: Coincident(g1,g2)
    c: Coincident(g2,g3)
    c: Coincident(g3,g0)
    c: Horizontal(g0)
    c: Horizontal(g2)
    c: Vertical(g1)
    c: Vertical(g3)
    c: DistanceY(g2) = 1590
    c: DistanceX(g2) = 0.1
    c: DistanceX(g1) = -14
    c: DistanceY(g0) = 485
    c: DistanceY(g3,g3) = 1105
FEATURE [PartDesign::Pad] Pad029
  Direction = (0,-1,2e-16)
  Length = 3
  Length2 = 10
  Placement = pos=(0,0,0) rot=(1,0,0;1.5708rad)
  Profile = -> Sketch205
  ReferenceAxis = -> Sketch205 [N_Axis]
  Suppressed = false
  Type = 0
FEATURE [PartDesign::Boolean] Boolean020
  BaseFeature = -> Pad029
  Group = -> [Compound060]
  Suppressed = false
  Type = 1
  UsePlacement = false
FEATURE [Sketcher::SketchObject] Sketch206
  AttachmentSupport = -> [XZ_Plane096]
  ExternalGeometry = -> [Sketch205]
  FullyConstrained = true
  MapMode = 5
  Placement = pos=(0,0,0) rot=(1,0,0;1.5708rad)
  sketch-geometry (13):
    g0: LineSegment StartX=-14 StartY=1590 StartZ=0 EndX=-6.95 EndY=1570 EndZ=0
    g1: LineSegment StartX=-6.95 StartY=1570 StartZ=0 EndX=0.1 EndY=1590 EndZ=0
    g2: LineSegment StartX=-14 StartY=485 StartZ=0 EndX=-6.95 EndY=505 EndZ=0
    g3: LineSegment StartX=-6.95 StartY=505 StartZ=0 EndX=0.1 EndY=485 EndZ=0
    g4: Circle CenterX=-6.95 CenterY=1570 CenterZ=0 NormalX=0 NormalY=0 NormalZ=1 AngleXU=0 Radius=1.7
    g5: Circle CenterX=-6.95 CenterY=1057.5 CenterZ=0 NormalX=0 NormalY=0 NormalZ=1 AngleXU=0 Radius=1.7
    g6: Circle CenterX=-6.95 CenterY=505 CenterZ=0 NormalX=0 NormalY=0 NormalZ=1 AngleXU=0 Radius=1.7
    g7: Circle CenterX=-6.95 CenterY=786.25 CenterZ=0 NormalX=0 NormalY=0 NormalZ=1 AngleXU=0 Radius=1.7
    g8: Circle CenterX=-6.95 CenterY=1288.75 CenterZ=0 NormalX=0 NormalY=0 NormalZ=1 AngleXU=0 Radius=1.7
    g9: LineSegment StartX=-6.95 StartY=505 StartZ=0 EndX=-6.95 EndY=771.25 EndZ=0
    g10: LineSegment StartX=-6.95 StartY=771.25 StartZ=0 EndX=-6.95 EndY=1037.5 EndZ=0
    g11: LineSegment StartX=-6.95 StartY=1037.5 StartZ=0 EndX=-6.95 EndY=1303.75 EndZ=0
    g12: LineSegment StartX=-6.95 StartY=1303.75 StartZ=0 EndX=-6.95 EndY=1570 EndZ=0
  constraints (34):
    c: Coincident(g-4,g0)
    c: Coincident(g0,g1)
    c: Coincident(g1,g-4)
    c: Coincident(g-3,g2)
    c: Coincident(g2,g3)
    c: Coincident(g3,g-3)
    c: Equal(g2,g3)
    c: Equal(g3,g0)
    c: Equal(g0,g1)
    c: DistanceY(g2,g2) = 20
    c: Coincident(g9,g2)
    c: Coincident(g11,g10)
    c: Coincident(g12,g0)
    c: Coincident(g4,g0)
    c: Coincident(g6,g2)
    c: Equal(g6,g5)
    c: Equal(g6,g4)
    c: Diameter(g6) = 3.4
    c: DistanceY(g10,g5) = 20
    c: Equal(g8,g7)
    c: Equal(g7,g6)
    c: Coincident(g9,g10)
    c: Vertical(g9)
    c: Vertical(g10)
    c: PointOnObject(g7,g9)
    c: Equal(g9,g10)
    c: Coincident(g11,g12)
    c: PointOnObject(g5,g11)
    c: PointOnObject(g8,g11)
    c: Equal(g11,g12)
    c: Equal(g10,g11)
    c: DistanceY(g8,g11) = 15
    c: DistanceY(g9,g7) = 15
    c: Vertical(g11)
FEATURE [PartDesign::Pocket] Pocket123
  BaseFeature = -> Boolean020
  Direction = (0,1,2e-16)
  Length = 5
  Length2 = 5
  Midplane = true
  Profile = -> Sketch206
  ReferenceAxis = -> Sketch206 [N_Axis]
  Suppressed = false
  Type = 1
FEATURE [PartDesign::Body] Body120  label="led_holder2"
  Group = -> [Sketch205,Pad029,Boolean020,Sketch206,Pocket123]
  Origin = -> Origin096
  Placement = pos=(0,3.2,0) rot=(0,0,1;3.14159rad)
  Tip = -> Pocket123
COMPONENT P6 — recipe-attached ("sector_plexiglass_material_0.30ansi", modeled in this document).
Construction recipe (the document's own serialized feature program — sketch geometry with constraints, then the solid features built on it; lengths are millimeters unless a unit is written):

FEATURE [PartDesign::SubShapeBinder] Binder128
  BindCopyOnChange = 0
  BindMode = 0
  ClaimChildren = true
  Context = -> Body121 [Binder128.]
  Fuse = false
  MakeFace = true
  OffsetFill = false
  OffsetIntersection = false
  OffsetJoinType = 0
  OffsetOpenResult = false
  PartialLoad = false
  Relative = false
  Support = -> [Compound061]
  _Version = 2
FEATURE [PartDesign::FeaturePython] BaseBend049  label="sector_plexiglass_BaseBend"  # WARN: FeaturePython — macro-defined, semantics opaque (R4)
  BendSide = 1
  BendSketch = -> Binder128
  MidPlane = false
  Reverse = false
  Suppressed = false
  length = 425
  radius = 1
  thickness = 1
FEATURE [PartDesign::CoordinateSystem] Local_CS004
  AttacherType = Attacher::AttachEngine3D
  AttachmentOffset = pos=(0,0,0) rot=(0,-1,0;1.5708rad)
  AttachmentSupport = -> [Binder128]
  MapMode = 7
  Placement = pos=(284.188,-181.72,0) rot=(0.131421,-0.700974,-0.700974;2.88025rad)
FEATURE [Sketcher::SketchObject] Sketch208
  AttachmentSupport = -> [Local_CS004]
  FullyConstrained = true
  MapMode = 5
  Placement = pos=(284.188,-181.72,0) rot=(-0.131421,0.700974,0.700974;3.40294rad)
  expr: Constraints[4] = <<plexiglass_bottom_fix_array>>.Step * 1 mm - <<plexiglass_bottom_fix_sketch>>.Constraints.length + 2 mm
  expr: Constraints[6] = <<plexiglass_bottom_fix_array>>.SpanStart - <<plexiglass_bottom_fix_array>>.Step * 1 mm / 2
  sketch-geometry (7):
    g0: LineSegment StartX=-12 StartY=-63.3333 StartZ=0 EndX=-12 EndY=15 EndZ=0
    g1: LineSegment StartX=-1 StartY=10 StartZ=0 EndX=-1 EndY=-58.3333 EndZ=0
    g2: GeomPoint X=-1 Y=-24.1667 Z=0
    g3: LineSegment StartX=-7 StartY=10 StartZ=0 EndX=-1 EndY=10 EndZ=0
    g4: LineSegment StartX=-1 StartY=-58.3333 StartZ=0 EndX=-7 EndY=-58.3333 EndZ=0
    g5: ArcOfCircle CenterX=-7 CenterY=15 CenterZ=0 NormalX=0 NormalY=0 NormalZ=1 AngleXU=0 Radius=5 StartAngle=3.14159 EndAngle=4.71239
    g6: ArcOfCircle CenterX=-7 CenterY=-63.3333 CenterZ=0 NormalX=0 NormalY=0 NormalZ=1 AngleXU=0 Radius=5 StartAngle=1.5708 EndAngle=3.14159
  constraints (17):
    c: Coincident(g3,g1)
    c: Coincident(g1,g4)
    c: Vertical(g0)
    c: Vertical(g1)
    c: DistanceY(g1,g1) = 68.3333
    c: Symmetric(g4,g3,g2)
    c: DistanceY(g2) = -24.1667
    c: Horizontal(g3)
    c: Horizontal(g4)
    c: Tangent(g5,g3) = -1.5708
    c: Tangent(g5,g0) = 1.5708
    c: Tangent(g6,g4) = -1.5708
    c: Tangent(g6,g0) = 1.5708
    c: Equal(g6,g5)
    c: Radius(g6) = 5
    c: Distance(g-1,g0) = 12
    c: Distance(g-1,g1) = 1
FEATURE [PartDesign::Pocket] Pocket124
  BaseFeature = -> BaseBend049
  Direction = (0.362233,-0.932087,0)
  Length = 5
  Length2 = 5
  Midplane = true
  Profile = -> Sketch208
  ReferenceAxis = -> Sketch208 [N_Axis]
  Suppressed = false
  Type = 1
FEATURE [PartDesign::LinearPattern] LinearPattern
  Direction = -> Z_Axis097
  Length = 591.667
  Mode = 1
  Occurrences = 6
  Offset = 118.333
  Suppressed = false
  expr: Length = <<plexiglass_bottom_fix_array>>.Step
  expr: Offset = <<plexiglass_bottom_fix_array>>.Step
FEATURE [PartDesign::Mirrored] Mirrored015
  MirrorPlane = -> YZ_Plane097
  Suppressed = false
FEATURE [PartDesign::MultiTransform] MultiTransform001
  BaseFeature = -> Pocket124
  Originals = -> [Pocket124]
  Suppressed = false
  Transformations = -> [LinearPattern,Mirrored015]
FEATURE [Sketcher::SketchObject] Sketch242
  AttachmentOffset = pos=(0,35,0) rot=(0,0,1;0rad)
  AttachmentSupport = -> [Local_CS004]
  FullyConstrained = true
  MapMode = 5
  Placement = pos=(284.188,-181.72,35) rot=(-0.131421,0.700974,0.700974;3.40294rad)
  sketch-geometry (3):
    g0: Circle CenterX=-6.5 CenterY=0 CenterZ=0 NormalX=0 NormalY=0 NormalZ=1 AngleXU=0 Radius=1.7
    g1: GeomPoint X=-12 Y=0 Z=0
    g2: GeomPoint X=-1 Y=0 Z=0
  constraints (6):
    c: Diameter(g0) = 3.4
    c: PointOnObject(g1,g-1)
    c: PointOnObject(g2,g-1)
    c: DistanceX(g2) = -1
    c: DistanceX(g1) = -12
    c: Symmetric(g2,g1,g0)
FEATURE [PartDesign::Pocket] Pocket134
  BaseFeature = -> MultiTransform001
  Direction = (0.362233,-0.932087,0)
  Length = 5
  Length2 = 5
  Midplane = true
  Profile = -> Sketch242
  ReferenceAxis = -> Sketch242 [N_Axis]
  Suppressed = false
  Type = 1
FEATURE [PartDesign::LinearPattern] LinearPattern001
  Direction = -> Z_Axis097
  Length = 355
  Mode = 0
  Occurrences = 2
  Offset = 355
  Suppressed = false
FEATURE [PartDesign::Mirrored] Mirrored019
  MirrorPlane = -> YZ_Plane097
  Suppressed = false
FEATURE [PartDesign::MultiTransform] MultiTransform
  BaseFeature = -> Pocket134
  Originals = -> [Pocket134]
  Suppressed = false
  Transformations = -> [LinearPattern001,Mirrored019]
FEATURE [PartDesign::Body] Body121  label="sector_plexiglass_material_0.30ansi"
  Group = -> [Binder128,BaseBend049,Sketch208,Local_CS004,Pocket124,MultiTransform001,LinearPattern,Mirrored015,Sketch242,Pocket134,MultiTransform,LinearPattern001,Mirrored019]
  Origin = -> Origin097
  Tip = -> MultiTransform
COMPONENT P7 — recipe-attached ("basin_limiter", modeled in this document).
Construction recipe (the document's own serialized feature program — sketch geometry with constraints, then the solid features built on it; lengths are millimeters unless a unit is written):

FEATURE [PartDesign::SubShapeBinder] Binder131
  BindCopyOnChange = 0
  BindMode = 0
  ClaimChildren = true
  Fuse = false
  MakeFace = true
  OffsetFill = false
  OffsetIntersection = false
  OffsetJoinType = 0
  OffsetOpenResult = false
  PartialLoad = false
  Placement = pos=(0,0,0) rot=(0,0,1;3.14159rad)
  Relative = false
  Support = -> [Compound064]
  _Version = 2
FEATURE [PartDesign::Pad] Pad030
  Direction = (0,0,1)
  Length = 3
  Length2 = 10
  Placement = pos=(0,0,0) rot=(0,0,1;3.14159rad)
  Profile = -> Binder131
  Refine = true
  Suppressed = false
  Type = 0
FEATURE [PartDesign::Boolean] Boolean022
  BaseFeature = -> Pad030
  Group = -> [Compound065]
  Refine = true
  Suppressed = false
  Type = 1
  UsePlacement = false
FEATURE [PartDesign::SubShapeBinder] Binder133
  BindCopyOnChange = 0
  BindMode = 0
  ClaimChildren = true
  Context = -> Body122 [Binder133.]
  Fuse = false
  MakeFace = true
  OffsetFill = false
  OffsetIntersection = false
  OffsetJoinType = 0
  OffsetOpenResult = false
  PartialLoad = false
  Relative = true
  Support = -> [Sketch210]
  _Version = 2
FEATURE [PartDesign::Body] Body122  label="basin_limiter"
  Group = -> [Binder131,Pad030,Boolean022,Binder133]
  Origin = -> Origin098
  Placement = pos=(0,0,21) rot=(0,0,1;0rad)
  Tip = -> Boolean022
COMPONENT P8 — recipe-attached ("Body", modeled in this document).
Construction recipe (the document's own serialized feature program — sketch geometry with constraints, then the solid features built on it; lengths are millimeters unless a unit is written):

FEATURE [Sketcher::SketchObject] Sketch223
  AttachmentOffset = pos=(0,0,0) rot=(0,1,0;0.523599rad)
  AttachmentSupport = -> [XZ_Plane102]
  FullyConstrained = true
  MapMode = 5
  Placement = pos=(0,0,0) rot=(0.935113,0.250563,0.250563;1.63783rad)
  expr: Constraints[15] = <<sleeve_outer_sketch>>.Constraints.flange_max_r + 1 mm
  expr: Constraints[16] = <<sleeve_outer_sketch>>.Constraints.max_r + 1 mm
  sketch-geometry (8):
    g0: ArcOfCircle CenterX=39.25 CenterY=3 CenterZ=0 NormalX=0 NormalY=0 NormalZ=1 AngleXU=0 Radius=3 StartAngle=3.14159 EndAngle=4.71239
    g1: LineSegment StartX=36.25 StartY=3 StartZ=0 EndX=36.25 EndY=48.4 EndZ=0
    g2: LineSegment StartX=36.25 StartY=48.4 StartZ=0 EndX=21.25 EndY=48.4 EndZ=0
    g3: LineSegment StartX=21.25 StartY=48.4 StartZ=0 EndX=21.25 EndY=40.4 EndZ=0
    g4: LineSegment StartX=0 StartY=0 StartZ=0 EndX=39.25 EndY=0 EndZ=0
    g5: LineSegment StartX=21.25 StartY=40.4 StartZ=0 EndX=0 EndY=40.4 EndZ=0
    g6: LineSegment StartX=0 StartY=40.4 StartZ=0 EndX=0 EndY=0 EndZ=0
    g7: GeomPoint X=21.25 Y=48.4 Z=0
  constraints (21):
    c: PointOnObject(g0,g-1)
    c: Vertical(g1)
    c: Coincident(g2,g1)
    c: Horizontal(g2)
    c: Vertical(g3)
    c: Tangent(g1,g0) = 1.5708
    c: Coincident(g4,g-1)
    c: Tangent(g4,g0) = -1.5708
    c: Radius(g0) = 3
    c: Coincident(g5,g3)
    c: PointOnObject(g5,g-2)
    c: Horizontal(g5)
    c: Coincident(g6,g5)
    c: Coincident(g6,g4)
    c: DistanceY(g6,g6) = 40.4
    c: DistanceX(g1) = 36.25
    c: DistanceX(g7) = 21.25
    c: DistanceY(g7,g3) = -8
    c: PointOnObject(g7,g2)
    c: PointOnObject(g7,g3)
    c: Coincident(g2,g3)
FEATURE [Sketcher::SketchObject] Sketch224
  AttachmentSupport = -> [XY_Plane102]
  FullyConstrained = true
  MapMode = 5
  expr: Constraints[10] = <<sleeve_outer_sketch>>.Constraints.max_r + 1 mm
  sketch-geometry (7):
    g0: LineSegment StartX=1.3e-15 StartY=21.4809 StartZ=0 EndX=0 EndY=0.46188 EndZ=0
    g1: LineSegment StartX=0 StartY=0.46188 StartZ=0 EndX=18.203 EndY=10.9714 EndZ=0
    g2: LineSegment StartX=0 StartY=0 StartZ=0 EndX=-0.2 EndY=0.34641 EndZ=0
    g3: LineSegment StartX=-0.2 StartY=0.34641 StartZ=0 EndX=0 EndY=0.46188 EndZ=0
    g4: ArcOfCircle CenterX=0 CenterY=0.46188 CenterZ=0 NormalX=0 NormalY=0 NormalZ=1 AngleXU=0 Radius=21.0191 StartAngle=0.648827 EndAngle=1.5708
    g5: ArcOfCircle CenterX=19.1382 CenterY=14.9754 CenterZ=0 NormalX=0 NormalY=0 NormalZ=1 AngleXU=0 Radius=3 StartAngle=3.79042 EndAngle=5.23599
    g6: LineSegment StartX=18.203 StartY=10.9714 StartZ=0 EndX=20.6382 EndY=12.3774 EndZ=0
  constraints (19):
    c: PointOnObject(g0,g-2)
    c: PointOnObject(g0,g-2)
    c: Coincident(g0,g1)
    c: Angle(g1) = 0.523599
    c: Distance(g-1,g1) = 0.4
    c: Coincident(g4,g0)
    c: Coincident(g2,g3)
    c: Coincident(g3,g0)
    c: Perpendicular(g3,g2)
    c: Parallel(g3,g1)
    c: Distance(g2,g1) = 21.25
    c: Coincident(g6,g1)
    c: Parallel(g6,g1)
    c: Tangent(g5,g4) = 1.5708
    c: PointOnObject(g1,g4)
    c: Coincident(g-1,g2)
    c: Coincident(g4,g0)
    c: Tangent(g6,g5) = -1.5708
    c: Radius(g5) = 3
FEATURE [PartDesign::Pad] Pad034
  Direction = (0.5,-0.866025,1e-16)
  Length = 0.4
  Length2 = 10
  Placement = pos=(0,0,0) rot=(1,0,0;1.5708rad)
  Profile = -> Sketch223
  ReferenceAxis = -> Sketch223 [N_Axis]
  Reversed = true
  Suppressed = false
  Type = 0
FEATURE [PartDesign::Pad] Pad035
  BaseFeature = -> Pad034
  Direction = (0,0,1)
  Length = 50
  Length2 = 10
  Placement = pos=(0,0,0) rot=(1,0,0;1.5708rad)
  Profile = -> Sketch224
  ReferenceAxis = -> Sketch224 [N_Axis]
  Suppressed = false
  Type = 0
FEATURE [PartDesign::Mirrored] Mirrored018
  BaseFeature = -> Pad035
  MirrorPlane = -> YZ_Plane102
  Originals = -> [Pad034,Pad035]
  Placement = pos=(0,0,0) rot=(1,0,0;1.5708rad)
  Suppressed = false
FEATURE [PartDesign::Body] Body125  label="Body"
  Group = -> [Sketch223,Sketch224,Pad034,Pad035,Mirrored018]
  Origin = -> Origin102
  Tip = -> Mirrored018
COMPONENT P9 — recipe-attached ("UV_driver_holder_material_0.30ansi", modeled in this document).
Construction recipe (the document's own serialized feature program — sketch geometry with constraints, then the solid features built on it; lengths are millimeters unless a unit is written):

FEATURE [PartDesign::SubShapeBinder] Binder149
  BindCopyOnChange = 0
  BindMode = 0
  ClaimChildren = true
  Context = -> <external composit_full_size3_composit_cut.FCStd>#Link026 [Binder149.]
  Fuse = false
  MakeFace = true
  OffsetFill = false
  OffsetIntersection = false
  OffsetJoinType = 0
  OffsetOpenResult = false
  PartialLoad = false
  Placement = pos=(0,0,0) rot=(1,0,0;1.5708rad)
  Relative = false
  Support = -> [Sketch225]
  _Version = 2
  expr: Support = <<UV_driver_holder_base_Sketch>>._self
FEATURE [PartDesign::FeaturePython] BaseBend050  label="UV_driver_holder_BaseBend"  # WARN: FeaturePython — macro-defined, semantics opaque (R4)
  BendSide = 0
  BendSketch = -> Binder149
  MidPlane = true
  Reverse = false
  Suppressed = false
  length = 20
  radius = 0.1
  thickness = 0.3
FEATURE [Sketcher::SketchObject] Sketch269
  AttachmentOffset = pos=(31.5,10,0) rot=(0,0,1;0rad)
  AttachmentSupport = -> [XY_Plane103]
  FullyConstrained = true
  MapMode = 5
  Placement = pos=(31.5,10,0) rot=(0,0,1;0rad)
  expr: .AttachmentOffset.Base.x = <<UV_driver_holder_base_Sketch>>.Constraints.total_width / 2
  expr: .AttachmentOffset.Base.y = <<UV_driver_holder_BaseBend>>.length / 2
  sketch-geometry (3):
    g0: LineSegment StartX=-3 StartY=0 StartZ=0 EndX=0 EndY=0 EndZ=0
    g1: LineSegment StartX=0 StartY=0 StartZ=0 EndX=0 EndY=-3 EndZ=0
    g2: ArcOfCircle CenterX=-3 CenterY=-3 CenterZ=0 NormalX=0 NormalY=0 NormalZ=1 AngleXU=0 Radius=3 StartAngle=1e-16 EndAngle=1.5708
  constraints (7):
    c: PointOnObject(g0,g-1)
    c: Coincident(g0,g-1)
    c: Coincident(g0,g1)
    c: PointOnObject(g1,g-2)
    c: Tangent(g2,g0) = 1.5708
    c: Tangent(g2,g1) = 1.5708
    c: Radius(g2) = 3
FEATURE [PartDesign::Pocket] Pocket145
  BaseFeature = -> BaseBend050
  Direction = (0,0,-1)
  Length = 5
  Length2 = 5
  Profile = -> Sketch269
  ReferenceAxis = -> Sketch269 [N_Axis]
  Reversed = true
  Suppressed = false
  Type = 0
FEATURE [PartDesign::Mirrored] Mirrored023
  MirrorPlane = -> YZ_Plane103
  Suppressed = false
FEATURE [PartDesign::Mirrored] Mirrored024
  MirrorPlane = -> XZ_Plane103
  Suppressed = false
FEATURE [PartDesign::MultiTransform] MultiTransform002
  BaseFeature = -> Pocket145
  Originals = -> [Pocket145]
  Suppressed = false
  Transformations = -> [Mirrored023,Mirrored024]
FEATURE [PartDesign::Boolean] Boolean052
  BaseFeature = -> MultiTransform002
  Group = -> [Compound104]
  Suppressed = false
  Type = 1
  UsePlacement = true
FEATURE [PartDesign::Body] Body126  label="UV_driver_holder_material_0.30ansi"
  Group = -> [BaseBend050,Binder149,Sketch269,Pocket145,MultiTransform002,Mirrored023,Mirrored024,Boolean052]
  Origin = -> Origin103
  Tip = -> Boolean052
COMPONENT P10 — recipe-attached ("bottom_bearing", modeled in this document).
Construction recipe (the document's own serialized feature program — sketch geometry with constraints, then the solid features built on it; lengths are millimeters unless a unit is written):

FEATURE [Sketcher::SketchObject] Sketch227  label="bottom_bearing_Sketch"
  AttachmentSupport = -> [XZ_Plane104]
  FullyConstrained = true
  MapMode = 5
  Placement = pos=(0,0,0) rot=(1,0,0;1.5708rad)
  sketch-geometry (4):
    g0: LineSegment StartX=37.5 StartY=0 StartZ=0 EndX=50 EndY=0 EndZ=0
    g1: LineSegment StartX=50 StartY=0 StartZ=0 EndX=50 EndY=19 EndZ=0
    g2: LineSegment StartX=50 StartY=19 StartZ=0 EndX=37.5 EndY=19 EndZ=0
    g3: LineSegment StartX=37.5 StartY=19 StartZ=0 EndX=37.5 EndY=0 EndZ=0
  constraints (12):
    c: Coincident(g0,g1)
    c: Coincident(g1,g2)
    c: Coincident(g2,g3)
    c: Coincident(g3,g0)
    c: Horizontal(g0)
    c: Horizontal(g2)
    c: Vertical(g1)
    c: Vertical(g3)
    c: PointOnObject(g0,g-1)
    c: DistanceY(g3,g3) = 19  'height'
    c: DistanceX(g0) = 37.5  'inner_r'
    c: DistanceX(g0) = 50  'outer_r'
FEATURE [PartDesign::Revolution] Revolution002
  Angle = 360
  Angle2 = 60
  Axis = (0,2e-16,1)
  Base = (0,0,0)
  Placement = pos=(0,0,0) rot=(1,0,0;1.5708rad)
  Profile = -> Sketch227
  ReferenceAxis = -> Sketch227 [V_Axis]
  Reversed = true
  Suppressed = false
  Type = 0
FEATURE [PartDesign::Body] Body127  label="bottom_bearing"
  Group = -> [Sketch227,Revolution002]
  Origin = -> Origin104
  Tip = -> Revolution002
COMPONENT P11 — recipe-attached ("bottom_caprolon", modeled in this document).
Construction recipe (the document's own serialized feature program — sketch geometry with constraints, then the solid features built on it; lengths are millimeters unless a unit is written):

FEATURE [Sketcher::SketchObject] Sketch228
  AttachmentSupport = -> [XZ_Plane105]
  FullyConstrained = true
  MapMode = 5
  Placement = pos=(0,0,0) rot=(1,0,0;1.5708rad)
  expr: Constraints[12] = <<bottom_bearing_Sketch>>.Constraints.inner_r - 0.5 mm
  expr: Constraints[13] = <<bottom_bearing_Sketch>>.Constraints.outer_r
  expr: Constraints[16] = 61.3 mm - <<bottom_bearing_Sketch>>.Constraints.height
  sketch-geometry (6):
    g0: LineSegment StartX=37 StartY=0 StartZ=0 EndX=37 EndY=5 EndZ=0
    g1: LineSegment StartX=37 StartY=5 StartZ=0 EndX=50 EndY=5 EndZ=0
    g2: LineSegment StartX=50 StartY=5 StartZ=0 EndX=50 EndY=47.3 EndZ=0
    g3: LineSegment StartX=50 StartY=47.3 StartZ=0 EndX=0 EndY=47.3 EndZ=0
    g4: LineSegment StartX=0 StartY=47.3 StartZ=0 EndX=0 EndY=0 EndZ=0
    g5: LineSegment StartX=0 StartY=0 StartZ=0 EndX=37 EndY=0 EndZ=0
  constraints (17):
    c: Vertical(g0)
    c: Coincident(g0,g1)
    c: Coincident(g1,g2)
    c: Vertical(g2)
    c: Coincident(g2,g3)
    c: Horizontal(g3)
    c: Coincident(g3,g4)
    c: Vertical(g4)
    c: Coincident(g4,g5)
    c: Coincident(g5,g0)
    c: Horizontal(g5)
    c: DistanceY(g0,g0) = 5
    c: DistanceX(g0) = 37
    c: DistanceX(g1) = 50
    c: Horizontal(g1)
    c: Coincident(g4,g-1)
    c: DistanceY(g2,g2) = 42.3
FEATURE [PartDesign::Revolution] Revolution003
  Angle = 360
  Angle2 = 60
  Axis = (0,2e-16,1)
  Base = (0,0,0)
  Placement = pos=(0,0,0) rot=(1,0,0;1.5708rad)
  Profile = -> Sketch228
  ReferenceAxis = -> Sketch228 [V_Axis]
  Reversed = true
  Suppressed = false
  Type = 0
FEATURE [PartDesign::Boolean] Boolean036
  BaseFeature = -> Revolution003
  Group = -> [Compound085]
  Suppressed = false
  Type = 1
  UsePlacement = false
FEATURE [PartDesign::Body] Body128  label="bottom_caprolon"
  Group = -> [Sketch228,Revolution003,Boolean036]
  Origin = -> Origin105
  Placement = pos=(0,0,14) rot=(0,0,1;0rad)
  Tip = -> Boolean036
COMPONENT P12 — recipe-attached ("wheel", modeled in this document).
Construction recipe (the document's own serialized feature program — sketch geometry with constraints, then the solid features built on it; lengths are millimeters unless a unit is written):

FEATURE [Sketcher::SketchObject] Sketch229
  AttachmentSupport = -> [XY_Plane106]
  FullyConstrained = true
  MapMode = 5
  sketch-geometry (13):
    g0: LineSegment StartX=-15.05 StartY=-24.05 StartZ=0 EndX=-15.05 EndY=24.05 EndZ=0
    g1: LineSegment StartX=-15.05 StartY=24.05 StartZ=0 EndX=15.05 EndY=24.05 EndZ=0
    g2: LineSegment StartX=15.05 StartY=24.05 StartZ=0 EndX=15.05 EndY=-24.05 EndZ=0
    g3: LineSegment StartX=15.05 StartY=-24.05 StartZ=0 EndX=-15.05 EndY=-24.05 EndZ=0
    g4: GeomPoint X=2e-16 Y=0 Z=0
    g5: Circle CenterX=15.05 CenterY=24.05 CenterZ=0 NormalX=0 NormalY=0 NormalZ=1 AngleXU=0 Radius=3.15
    g6: Circle CenterX=-15.05 CenterY=24.05 CenterZ=0 NormalX=0 NormalY=0 NormalZ=1 AngleXU=0 Radius=3.15
    g7: Circle CenterX=-15.05 CenterY=-24.05 CenterZ=0 NormalX=0 NormalY=0 NormalZ=1 AngleXU=0 Radius=3.15
    g8: Circle CenterX=15.05 CenterY=-24.05 CenterZ=0 NormalX=0 NormalY=0 NormalZ=1 AngleXU=0 Radius=3.15
    g9: GeomPoint X=-18.2 Y=24.05 Z=0
    g10: GeomPoint X=18.2 Y=24.05 Z=0
    g11: GeomPoint X=15.05 Y=-27.2 Z=0
    g12: GeomPoint X=15.05 Y=27.2 Z=0
  constraints (28):
    c: Coincident(g0,g1)
    c: Coincident(g1,g2)
    c: Coincident(g2,g3)
    c: Coincident(g3,g0)
    c: Horizontal(g1)
    c: Horizontal(g3)
    c: Vertical(g0)
    c: Vertical(g2)
    c: Symmetric(g1,g0,g4)
    c: Coincident(g4,g-1)
    c: Coincident(g5,g1)
    c: Coincident(g6,g0)
    c: Coincident(g7,g0)
    c: Coincident(g8,g2)
    c: PointOnObject(g9,g6)
    c: PointOnObject(g10,g5)
    c: PointOnObject(g11,g8)
    c: PointOnObject(g12,g5)
    c: Vertical(g5,g12)
    c: Horizontal(g5,g10)
    c: Horizontal(g6,g9)
    c: Vertical(g8,g11)
    c: Equal(g5,g6)
    c: Equal(g6,g7)
    c: Equal(g7,g8)
    c: DistanceX(g9,g10) = 36.4
    c: DistanceY(g11,g12) = 54.4
    c: Diameter(g5) = 6.3
FEATURE [Sketcher::SketchObject] Sketch230
  AttachmentSupport = -> [XY_Plane106]
  FullyConstrained = true
  MapMode = 5
  sketch-geometry (5):
    g0: LineSegment StartX=-22.5 StartY=-30 StartZ=0 EndX=-22.5 EndY=30 EndZ=0
    g1: LineSegment StartX=-22.5 StartY=30 StartZ=0 EndX=22.5 EndY=30 EndZ=0
    g2: LineSegment StartX=22.5 StartY=30 StartZ=0 EndX=22.5 EndY=-30 EndZ=0
    g3: LineSegment StartX=22.5 StartY=-30 StartZ=0 EndX=-22.5 EndY=-30 EndZ=0
    g4: GeomPoint X=0 Y=0 Z=0
  constraints (12):
    c: Coincident(g0,g1)
    c: Coincident(g1,g2)
    c: Coincident(g2,g3)
    c: Coincident(g3,g0)
    c: Horizontal(g1)
    c: Horizontal(g3)
    c: Vertical(g0)
    c: Vertical(g2)
    c: Symmetric(g1,g0,g4)
    c: Coincident(g4,g-1)
    c: DistanceY(g2,g2) = 60
    c: DistanceX(g1,g1) = 45
FEATURE [PartDesign::Pad] Pad036
  Direction = (0,0,1)
  Length = 60.3
  Length2 = 10
  Profile = -> Sketch230
  ReferenceAxis = -> Sketch230 [N_Axis]
  Suppressed = false
  Type = 0
FEATURE [PartDesign::Body] Body129  label="wheel"
  Group = -> [Sketch229,Sketch230,Pad036]
  Origin = -> Origin106
  Tip = -> Pad036
COMPONENT P13 — recipe-attached ("Body130", modeled in this document).
Construction recipe (the document's own serialized feature program — sketch geometry with constraints, then the solid features built on it; lengths are millimeters unless a unit is written):

FEATURE [PartDesign::SubShapeBinder] Binder136
  BindCopyOnChange = 0
  BindMode = 0
  ClaimChildren = true
  Context = -> Body130 [Binder136.]
  Fuse = false
  MakeFace = true
  OffsetFill = false
  OffsetIntersection = false
  OffsetJoinType = 0
  OffsetOpenResult = false
  PartialLoad = false
  Relative = false
  Support = -> [Connect004]
  _Version = 2
FEATURE [PartDesign::Pad] Pad037
  Direction = (0,0,1)
  Length = 1
  Length2 = 10
  Profile = -> Binder136
  Suppressed = false
  Type = 0
FEATURE [PartDesign::Boolean] Boolean037
  BaseFeature = -> Pad037
  Group = -> [Compound086]
  Refine = true
  Suppressed = false
  Type = 0
  UsePlacement = false
FEATURE [PartDesign::Boolean] Boolean038
  BaseFeature = -> Boolean037
  Group = -> [Populate053]
  Suppressed = false
  Type = 1
  UsePlacement = false
FEATURE [PartDesign::Body] Body130
  Group = -> [Binder136,Pad037,Boolean037,Boolean038]
  Origin = -> Origin107
  Tip = -> Boolean038
COMPONENT P14 — recipe-attached ("small_bearing", modeled in this document).
Construction recipe (the document's own serialized feature program — sketch geometry with constraints, then the solid features built on it; lengths are millimeters unless a unit is written):

FEATURE [Sketcher::SketchObject] Sketch233  label="small_bearing_Sketch"
  AttachmentSupport = -> [XZ_Plane108]
  FullyConstrained = true
  MapMode = 5
  Placement = pos=(0,0,0) rot=(1,0,0;1.5708rad)
  sketch-geometry (4):
    g0: LineSegment StartX=6 StartY=0 StartZ=0 EndX=13 EndY=0 EndZ=0
    g1: LineSegment StartX=13 StartY=0 StartZ=0 EndX=13 EndY=8.9 EndZ=0
    g2: LineSegment StartX=13 StartY=8.9 StartZ=0 EndX=6 EndY=8.9 EndZ=0
    g3: LineSegment StartX=6 StartY=8.9 StartZ=0 EndX=6 EndY=0 EndZ=0
  constraints (12):
    c: Coincident(g0,g1)
    c: Coincident(g1,g2)
    c: Coincident(g2,g3)
    c: Coincident(g3,g0)
    c: Horizontal(g0)
    c: Horizontal(g2)
    c: Vertical(g1)
    c: Vertical(g3)
    c: PointOnObject(g0,g-1)
    c: DistanceY(g3,g3) = 8.9
    c: DistanceX(g0) = 6
    c: DistanceX(g0) = 13
FEATURE [PartDesign::Revolution] Revolution004
  Angle = 360
  Angle2 = 60
  Axis = (0,2e-16,1)
  Base = (0,0,0)
  Placement = pos=(0,0,0) rot=(1,0,0;1.5708rad)
  Profile = -> Sketch233
  ReferenceAxis = -> Sketch233 [V_Axis]
  Reversed = true
  Suppressed = false
  Type = 0
FEATURE [PartDesign::Body] Body131  label="small_bearing"
  Group = -> [Sketch233,Revolution004]
  Origin = -> Origin108
  Tip = -> Revolution004
COMPONENT P15 — recipe-attached ("sleeve_outer2", modeled in this document).
Construction recipe (the document's own serialized feature program — sketch geometry with constraints, then the solid features built on it; lengths are millimeters unless a unit is written):

FEATURE [Sketcher::SketchObject] Sketch234  label="sleeve_outer_sketch001"
  AttachmentSupport = -> [XZ_Plane110]
  FullyConstrained = true
  MapMode = 5
  Placement = pos=(0,0,0) rot=(1,0,0;1.5708rad)
  expr: Constraints[13] = <<sleeve_inner_sketch001>>.Constraints.outer_r + 0.25 mm
  sketch-geometry (6):
    g0: LineSegment StartX=13.25 StartY=74.7 StartZ=0 EndX=13.25 EndY=0 EndZ=0
    g1: LineSegment StartX=13.25 StartY=0 StartZ=0 EndX=35.25 EndY=0 EndZ=0
    g2: LineSegment StartX=35.25 StartY=0 StartZ=0 EndX=35.25 EndY=7 EndZ=0
    g3: LineSegment StartX=35.25 StartY=7 StartZ=0 EndX=20.25 EndY=7 EndZ=0
    g4: LineSegment StartX=20.25 StartY=7 StartZ=0 EndX=20.25 EndY=74.7 EndZ=0
    g5: LineSegment StartX=20.25 StartY=74.7 StartZ=0 EndX=13.25 EndY=74.7 EndZ=0
  constraints (20):
    c: PointOnObject(g0,g-1)
    c: Vertical(g0)
    c: Coincident(g0,g1)
    c: PointOnObject(g1,g-1)
    c: Coincident(g1,g2)
    c: Vertical(g2)
    c: Coincident(g2,g3)
    c: Horizontal(g3)
    c: Coincident(g3,g4)
    c: Vertical(g4)
    c: Coincident(g4,g5)
    c: Coincident(g5,g0)
    c: Horizontal(g5)
    c: DistanceX(g0) = 13.25
    c: DistanceX(g5,g5) = 7
    c: DistanceX(g3,g3) = 15
    c: DistanceY(g2,g2) = 7  'flange_height'
    c: DistanceY(g0,g0) = 74.7
    c: DistanceX(g3) = 20.25  'max_r'
    c: DistanceX(g1) = 35.25  'flange_max_r'
FEATURE [PartDesign::Revolution] Revolution006
  Angle = 360
  Angle2 = 60
  Axis = (0,2e-16,1)
  Base = (0,0,0)
  Placement = pos=(0,0,0) rot=(1,0,0;1.5708rad)
  Profile = -> Sketch234
  ReferenceAxis = -> Sketch234 [V_Axis]
  Reversed = true
  Suppressed = false
  Type = 0
FEATURE [PartDesign::Boolean] Boolean039
  BaseFeature = -> Revolution006
  Group = -> [Compound087]
  Suppressed = false
  Type = 1
  UsePlacement = false
FEATURE [PartDesign::CoordinateSystem] Local_CS035  label="sleeve2_outer_flange_LCS"
  AttacherType = Attacher::AttachEngine3D
  AttachmentSupport = -> [XY_Plane110]
  MapMode = 5
FEATURE [PartDesign::CoordinateSystem] Local_CS036  label="sleeve2_outer_end_LCS"
  AttacherType = Attacher::AttachEngine3D
  AttachmentOffset = pos=(0,0,74.7) rot=(0,0,1;0rad)
  AttachmentSupport = -> [XY_Plane110]
  MapMode = 5
  Placement = pos=(0,0,74.7) rot=(0,0,1;0rad)
FEATURE [PartDesign::Body] Body132  label="sleeve_outer2"
  Group = -> [Sketch234,Revolution006,Boolean039,Local_CS035,Local_CS036]
  Origin = -> Origin110
  Tip = -> Boolean039
COMPONENT P16 — recipe-attached ("sleeve_inner2", modeled in this document).
Construction recipe (the document's own serialized feature program — sketch geometry with constraints, then the solid features built on it; lengths are millimeters unless a unit is written):

FEATURE [Sketcher::SketchObject] Sketch235  label="sleeve_inner_sketch001"
  AttachmentSupport = -> [XZ_Plane101]
  FullyConstrained = true
  MapMode = 5
  Placement = pos=(0,0,0) rot=(1,0,0;1.5708rad)
  sketch-geometry (6):
    g0: LineSegment StartX=5 StartY=83.7 StartZ=0 EndX=5 EndY=0 EndZ=0
    g1: LineSegment StartX=5 StartY=0 StartZ=0 EndX=33 EndY=0 EndZ=0
    g2: LineSegment StartX=33 StartY=0 StartZ=0 EndX=33 EndY=5 EndZ=0
    g3: LineSegment StartX=33 StartY=5 StartZ=0 EndX=13 EndY=5 EndZ=0
    g4: LineSegment StartX=13 StartY=5 StartZ=0 EndX=13 EndY=83.7 EndZ=0
    g5: LineSegment StartX=13 StartY=83.7 StartZ=0 EndX=5 EndY=83.7 EndZ=0
  constraints (19):
    c: PointOnObject(g0,g-1)
    c: Vertical(g0)
    c: Coincident(g0,g1)
    c: PointOnObject(g1,g-1)
    c: Coincident(g1,g2)
    c: Vertical(g2)
    c: Coincident(g2,g3)
    c: Horizontal(g3)
    c: Coincident(g3,g4)
    c: Vertical(g4)
    c: Coincident(g4,g5)
    c: Coincident(g5,g0)
    c: Horizontal(g5)
    c: DistanceX(g0) = 5  'inner_r'
    c: DistanceX(g0,g3) = 8
    c: DistanceY(g2,g2) = 5
    c: DistanceX(g3,g3) = 20
    c: DistanceX(g3) = 13  'outer_r'
    c: DistanceY(g0) = 83.7
FEATURE [PartDesign::Revolution] Revolution005
  Angle = 360
  Angle2 = 60
  Axis = (0,2e-16,1)
  Base = (0,0,0)
  Placement = pos=(0,0,0) rot=(1,0,0;1.5708rad)
  Profile = -> Sketch235
  ReferenceAxis = -> Sketch235 [V_Axis]
  Reversed = true
  Suppressed = false
  Type = 0
FEATURE [PartDesign::Boolean] Boolean040
  BaseFeature = -> Revolution005
  Group = -> [Compound088]
  Suppressed = false
  Type = 1
  UsePlacement = false
FEATURE [PartDesign::CoordinateSystem] Local_CS033  label="sleeve_inner2_flange_top_LCS"
  AttacherType = Attacher::AttachEngine3D
  AttachmentOffset = pos=(0,0,5) rot=(0,0,1;0rad)
  AttachmentSupport = -> [XY_Plane101]
  MapMode = 5
  Placement = pos=(0,0,5) rot=(0,0,1;0rad)
FEATURE [PartDesign::CoordinateSystem] Local_CS034  label="sleeve_inner2_end_LCS"
  AttacherType = Attacher::AttachEngine3D
  AttachmentOffset = pos=(0,0,83.7) rot=(0,0,1;0rad)
  AttachmentSupport = -> [XY_Plane101]
  MapMode = 5
  Placement = pos=(0,0,83.7) rot=(0,0,1;0rad)
FEATURE [PartDesign::Body] Body133  label="sleeve_inner2"
  Group = -> [Sketch235,Revolution005,Boolean040,Local_CS033,Local_CS034]
  Origin = -> Origin111
  Tip = -> Boolean040
COMPONENT P17 — recipe-attached ("wire_holder_material_0.30ansi", modeled in this document).
Construction recipe (the document's own serialized feature program — sketch geometry with constraints, then the solid features built on it; lengths are millimeters unless a unit is written):

FEATURE [PartDesign::SubShapeBinder] Binder137
  BindCopyOnChange = 0
  BindMode = 0
  ClaimChildren = true
  Context = -> Body134 [Binder137.]
  Fuse = false
  MakeFace = true
  OffsetFill = false
  OffsetIntersection = false
  OffsetJoinType = 0
  OffsetOpenResult = false
  PartialLoad = false
  Relative = false
  Support = -> [Sketch236]
  _Version = 2
FEATURE [PartDesign::FeaturePython] BaseBend051  # WARN: FeaturePython — macro-defined, semantics opaque (R4)
  BendSide = 0
  BendSketch = -> Binder137
  MidPlane = false
  Reverse = false
  Suppressed = false
  length = 830
  radius = 0.1
  thickness = 0.3
FEATURE [PartDesign::Boolean] Boolean041
  BaseFeature = -> BaseBend051
  Group = -> [Compound089]
  Suppressed = false
  Type = 1
  UsePlacement = false
FEATURE [PartDesign::Body] Body134  label="wire_holder_material_0.30ansi"
  Group = -> [Binder137,BaseBend051,Boolean041]
  Origin = -> Origin112
  Tip = -> Boolean041
COMPONENT P18 — recipe-attached ("wire_holder", modeled in this document).
Construction recipe (the document's own serialized feature program — sketch geometry with constraints, then the solid features built on it; lengths are millimeters unless a unit is written):

FEATURE [PartDesign::SubShapeBinder] Binder138
  BindCopyOnChange = 0
  BindMode = 0
  ClaimChildren = true
  Context = -> Body135 [Binder138.]
  Fuse = false
  MakeFace = true
  OffsetFill = false
  OffsetIntersection = false
  OffsetJoinType = 0
  OffsetOpenResult = false
  PartialLoad = false
  Relative = true
  Support = -> [Sketch237]
  _Version = 2
FEATURE [PartDesign::Pad] Pad038
  Direction = (0,0,1)
  Length = 10
  Length2 = 10
  Profile = -> Binder138 [Face1]
  Suppressed = false
  Type = 0
FEATURE [PartDesign::Boolean] Boolean042
  BaseFeature = -> Pad038
  Group = -> [Compound090]
  Suppressed = false
  Type = 1
  UsePlacement = false
FEATURE [PartDesign::Body] Body135  label="wire_holder"
  Group = -> [Binder138,Pad038,Boolean042]
  Origin = -> Origin113
  Tip = -> Boolean042
COMPONENT P19 — recipe-attached ("Body136", modeled in this document).
Construction recipe (the document's own serialized feature program — sketch geometry with constraints, then the solid features built on it; lengths are millimeters unless a unit is written):

FEATURE [Sketcher::SketchObject] Sketch238
  AttachmentSupport = -> [XY_Plane113]
  FullyConstrained = true
  MapMode = 5
  sketch-geometry (10):
    g0: LineSegment StartX=-10 StartY=-23.5 StartZ=0 EndX=10 EndY=-23.5 EndZ=0
    g1: LineSegment StartX=15 StartY=-18.5 StartZ=0 EndX=15 EndY=18.5 EndZ=0
    g2: LineSegment StartX=10 StartY=23.5 StartZ=0 EndX=-10 EndY=23.5 EndZ=0
    g3: LineSegment StartX=-15 StartY=18.5 StartZ=0 EndX=-15 EndY=-18.5 EndZ=0
    g4: ArcOfCircle CenterX=-10 CenterY=-18.5 CenterZ=0 NormalX=0 NormalY=0 NormalZ=1 AngleXU=0 Radius=5 StartAngle=3.14159 EndAngle=4.71239
    g5: ArcOfCircle CenterX=10 CenterY=-18.5 CenterZ=0 NormalX=0 NormalY=0 NormalZ=1 AngleXU=0 Radius=5 StartAngle=4.71239 EndAngle=6.28319
    g6: ArcOfCircle CenterX=10 CenterY=18.5 CenterZ=0 NormalX=0 NormalY=0 NormalZ=1 AngleXU=0 Radius=5 StartAngle=2.76279e-11 EndAngle=1.5708
    g7: ArcOfCircle CenterX=-10 CenterY=18.5 CenterZ=0 NormalX=0 NormalY=0 NormalZ=1 AngleXU=0 Radius=5 StartAngle=1.5708 EndAngle=3.14159
    g8: GeomPoint X=-15 Y=-23.5 Z=0
    g9: GeomPoint X=15 Y=23.5 Z=0
  constraints (23):
    c: Tangent(g0,g4) = -1.5708
    c: Tangent(g0,g5) = -1.5708
    c: Tangent(g1,g5) = -1.5708
    c: Tangent(g1,g6) = -1.5708
    c: Tangent(g2,g6) = -1.5708
    c: Tangent(g2,g7) = -1.5708
    c: Tangent(g3,g7) = -1.5708
    c: Tangent(g3,g4) = -1.5708
    c: Horizontal(g0)
    c: Horizontal(g2)
    c: Vertical(g1)
    c: Vertical(g3)
    c: Equal(g4,g5)
    c: Equal(g5,g6)
    c: Equal(g6,g7)
    c: PointOnObject(g8,g0)
    c: PointOnObject(g8,g3)
    c: PointOnObject(g9,g1)
    c: PointOnObject(g9,g2)
    c: Distance(g1,g3) = 30
    c: Distance(g0,g2) = 47
    c: Radius(g5) = 5
    c: Symmetric(g8,g9,g-1)
FEATURE [PartDesign::Pad] Pad039
  Direction = (0,0,1)
  Length = 1.5
  Length2 = 10
  Profile = -> Sketch238
  ReferenceAxis = -> Sketch238 [N_Axis]
  Suppressed = false
  Type = 0
FEATURE [PartDesign::SubShapeBinder] Binder139
  BindCopyOnChange = 0
  BindMode = 0
  ClaimChildren = true
  Fuse = false
  MakeFace = true
  OffsetFill = false
  OffsetIntersection = false
  OffsetJoinType = 0
  OffsetOpenResult = false
  PartialLoad = false
  Relative = false
  Support = -> [Sketch239]
  _Version = 2
FEATURE [PartDesign::Pocket] Pocket133
  BaseFeature = -> Pad039
  Direction = (0,0,-1)
  Length = 5
  Length2 = 5
  Midplane = true
  Profile = -> Binder139
  Suppressed = false
  Type = 1
FEATURE [PartDesign::Body] Body136
  Group = -> [Sketch238,Pad039,Binder139,Pocket133]
  Origin = -> Origin114
  Tip = -> Pocket133
COMPONENT P20 — recipe-attached ("wheel_proxy", modeled in this document).
Construction recipe (the document's own serialized feature program — sketch geometry with constraints, then the solid features built on it; lengths are millimeters unless a unit is written):

FEATURE [PartDesign::SubShapeBinder] Binder140
  BindCopyOnChange = 0
  BindMode = 0
  ClaimChildren = true
  Fuse = false
  MakeFace = true
  OffsetFill = false
  OffsetIntersection = false
  OffsetJoinType = 0
  OffsetOpenResult = false
  PartialLoad = false
  Relative = false
  Support = -> [Sketch240]
  _Version = 2
FEATURE [PartDesign::Pad] Pad040
  Direction = (0,0,1)
  Length = 3
  Length2 = 10
  Profile = -> Binder140
  Suppressed = false
  Type = 0
FEATURE [PartDesign::Boolean] Boolean043
  BaseFeature = -> Pad040
  Group = -> [Compound091]
  Suppressed = false
  Type = 1
  UsePlacement = false
FEATURE [PartDesign::Body] Body137  label="wheel_proxy"
  Group = -> [Binder140,Pad040,Boolean043]
  Origin = -> Origin115
  Tip = -> Boolean043
COMPONENT P21 — recipe-attached ("Body138", modeled in this document).
Construction recipe (the document's own serialized feature program — sketch geometry with constraints, then the solid features built on it; lengths are millimeters unless a unit is written):

FEATURE [Sketcher::SketchObject] Sketch243
  AttachmentSupport = -> [XY_Plane115]
  FullyConstrained = true
  MapMode = 5
  expr: Constraints[1] = <<bottom_bearing_Sketch>>.Constraints.outer_r * 2 + 50 mm
  sketch-geometry (1):
    g0: Circle CenterX=0 CenterY=0 CenterZ=0 NormalX=0 NormalY=0 NormalZ=1 AngleXU=0 Radius=75
  constraints (2):
    c: Coincident(g0,g-1)
    c: Diameter(g0) = 150
FEATURE [PartDesign::Pad] Pad041
  Direction = (0,0,1)
  Length = 18
  Length2 = 10
  Profile = -> Sketch243
  ReferenceAxis = -> Sketch243 [N_Axis]
  Suppressed = false
  Type = 0
FEATURE [Sketcher::SketchObject] Sketch244
  AttachmentOffset = pos=(0,0,18) rot=(0,0,1;0rad)
  AttachmentSupport = -> [XY_Plane115]
  FullyConstrained = true
  MapMode = 5
  Placement = pos=(0,0,18) rot=(0,0,1;0rad)
  expr: .AttachmentOffset.Base.z = <<Pad041>>.Length
  expr: .Constraints.inner_r = <<bottom_bearing_Sketch>>.Constraints.inner_r * 2 - 1 mm
  expr: .Constraints.outer_r = <<bottom_bearing_Sketch>>.Constraints.outer_r * 2 + 1 mm
  sketch-geometry (2):
    g0: Circle CenterX=0 CenterY=0 CenterZ=0 NormalX=0 NormalY=0 NormalZ=1 AngleXU=0 Radius=37
    g1: Circle CenterX=0 CenterY=0 CenterZ=0 NormalX=0 NormalY=0 NormalZ=1 AngleXU=0 Radius=50.5
  constraints (4):
    c: Coincident(g0,g-1)
    c: Coincident(g1,g0)
    c: Diameter(g0) = 74  'inner_r'
    c: Diameter(g1) = 101  'outer_r'
FEATURE [PartDesign::Pocket] Pocket135
  BaseFeature = -> Pad041
  Direction = (0,0,-1)
  Length = 5
  Length2 = 5
  Profile = -> Sketch244
  ReferenceAxis = -> Sketch244 [N_Axis]
  Suppressed = false
  Type = 0
FEATURE [Sketcher::SketchObject] Sketch245
  AttachmentSupport = -> [XY_Plane115]
  FullyConstrained = true
  MapMode = 5
  sketch-geometry (1):
    g0: Circle CenterX=0 CenterY=0 CenterZ=0 NormalX=0 NormalY=0 NormalZ=1 AngleXU=0 Radius=5.25
  constraints (2):
    c: Coincident(g0,g-1)
    c: Diameter(g0) = 10.5
FEATURE [PartDesign::Boolean] Boolean044
  BaseFeature = -> Pocket135
  Group = -> [Fusion]
  Suppressed = false
  Type = 1
  UsePlacement = false
FEATURE [PartDesign::Body] Body138
  Group = -> [Sketch243,Pad041,Sketch244,Pocket135,Sketch245,Boolean044]
  Origin = -> Origin116
  Tip = -> Boolean044
COMPONENT P22 — recipe-attached ("Body139", modeled in this document).
Construction recipe (the document's own serialized feature program — sketch geometry with constraints, then the solid features built on it; lengths are millimeters unless a unit is written):

FEATURE [Sketcher::SketchObject] Sketch246
  AttachmentSupport = -> [XY_Plane116]
  FullyConstrained = true
  MapMode = 5
  sketch-geometry (7):
    g0: LineSegment StartX=7.50555 StartY=0 StartZ=0 EndX=3.75278 EndY=6.5 EndZ=0
    g1: LineSegment StartX=3.75278 StartY=6.5 StartZ=0 EndX=-3.75278 EndY=6.5 EndZ=0
    g2: LineSegment StartX=-3.75278 StartY=6.5 StartZ=0 EndX=-7.50555 EndY=4.3228e-12 EndZ=0
    g3: LineSegment StartX=-7.50555 StartY=4.3229e-12 StartZ=0 EndX=-3.75278 EndY=-6.5 EndZ=0
    g4: LineSegment StartX=-3.75278 StartY=-6.5 StartZ=0 EndX=3.75278 EndY=-6.5 EndZ=0
    g5: LineSegment StartX=3.75278 StartY=-6.5 StartZ=0 EndX=7.50555 EndY=0 EndZ=0
    g6: Circle CenterX=0 CenterY=0 CenterZ=0 NormalX=0 NormalY=0 NormalZ=1 AngleXU=0 Radius=7.50555
  constraints (16):
    c: Coincident(g0,g1)
    c: Coincident(g1,g2)
    c: Coincident(g2,g3)
    c: Coincident(g3,g4)
    c: Coincident(g4,g5)
    c: Coincident(g5,g0)
    c: Equal(g0, g1-g5) x5
    c: PointOnObject(g0,g6)
    c: PointOnObject(g1,g6)
    c: PointOnObject(g2,g6)
    c: PointOnObject(g3,g6)
    c: PointOnObject(g4,g6)
    c: PointOnObject(g5,g6)
    c: Coincident(g6,g-1)
    c: PointOnObject(g5,g-1)
    c: DistanceY(g4,g0) = 13
FEATURE [PartDesign::Pad] Pad042
  Direction = (0,0,1)
  Length = 5
  Length2 = 10
  Profile = -> Sketch246
  ReferenceAxis = -> Sketch246 [N_Axis]
  Suppressed = false
  Type = 0
FEATURE [Sketcher::SketchObject] Sketch247
  AttachmentSupport = -> [XY_Plane116]
  FullyConstrained = true
  MapMode = 5
  sketch-geometry (1):
    g0: Circle CenterX=0 CenterY=0 CenterZ=0 NormalX=0 NormalY=0 NormalZ=1 AngleXU=0 Radius=4.25
  constraints (2):
    c: Coincident(g0,g-1)
    c: Diameter(g0) = 8.5
FEATURE [PartDesign::Pad] Pad043
  BaseFeature = -> Pad042
  Direction = (0,0,1)
  Length = 20
  Length2 = 10
  Profile = -> Sketch247
  ReferenceAxis = -> Sketch247 [N_Axis]
  Suppressed = false
  Type = 0
FEATURE [PartDesign::Body] Body139
  Group = -> [Sketch246,Pad042,Sketch247,Pad043]
  Origin = -> Origin117
  Placement = pos=(60,0,0) rot=(0,0,1;0rad)
  Tip = -> Pad043
  expr: .Placement.Base.x = <<bottom_bearing_Sketch>>.Constraints.outer_r + 10 mm
COMPONENT P23 — recipe-attached ("Body140", modeled in this document).
Construction recipe (the document's own serialized feature program — sketch geometry with constraints, then the solid features built on it; lengths are millimeters unless a unit is written):

FEATURE [Sketcher::SketchObject] Sketch248
  AttachmentOffset = pos=(0,0,18) rot=(0,0,1;0rad)
  AttachmentSupport = -> [XY_Plane117]
  FullyConstrained = true
  MapMode = 5
  Placement = pos=(0,0,18) rot=(0,0,1;0rad)
  expr: .AttachmentOffset.Base.z = <<Pad044>>.Length
  expr: .Constraints.inner_r = <<bottom_bearing_Sketch>>.Constraints.inner_r * 2 - 1 mm
  expr: .Constraints.outer_r = <<bottom_bearing_Sketch>>.Constraints.outer_r * 2 + 1 mm
  sketch-geometry (2):
    g0: Circle CenterX=0 CenterY=0 CenterZ=0 NormalX=0 NormalY=0 NormalZ=1 AngleXU=0 Radius=37
    g1: Circle CenterX=0 CenterY=0 CenterZ=0 NormalX=0 NormalY=0 NormalZ=1 AngleXU=0 Radius=50.5
  constraints (4):
    c: Coincident(g0,g-1)
    c: Coincident(g1,g0)
    c: Diameter(g0) = 74  'inner_r'
    c: Diameter(g1) = 101  'outer_r'
FEATURE [Sketcher::SketchObject] Sketch249
  AttachmentSupport = -> [XY_Plane117]
  FullyConstrained = true
  MapMode = 5
  expr: Constraints[1] = <<bottom_bearing_Sketch>>.Constraints.outer_r * 2 + 50 mm
  sketch-geometry (1):
    g0: Circle CenterX=0 CenterY=0 CenterZ=0 NormalX=0 NormalY=0 NormalZ=1 AngleXU=0 Radius=75
  constraints (2):
    c: Coincident(g0,g-1)
    c: Diameter(g0) = 150
FEATURE [PartDesign::Pad] Pad044
  Direction = (0,0,1)
  Length = 18
  Length2 = 10
  Profile = -> Sketch249
  ReferenceAxis = -> Sketch249 [N_Axis]
  Suppressed = false
  Type = 0
FEATURE [Sketcher::SketchObject] Sketch250
  AttachmentSupport = -> [XY_Plane117]
  FullyConstrained = true
  MapMode = 5
  sketch-geometry (1):
    g0: Circle CenterX=0 CenterY=0 CenterZ=0 NormalX=0 NormalY=0 NormalZ=1 AngleXU=0 Radius=5.25
  constraints (2):
    c: Coincident(g0,g-1)
    c: Diameter(g0) = 10.5
FEATURE [PartDesign::Pocket] Pocket136
  BaseFeature = -> Pad044
  Direction = (0,0,-1)
  Length = 5
  Length2 = 5
  Profile = -> Sketch248
  ReferenceAxis = -> Sketch248 [N_Axis]
  Suppressed = false
  Type = 0
FEATURE [PartDesign::Boolean] Boolean045
  BaseFeature = -> Pocket136
  Group = -> [Fusion001]
  Suppressed = false
  Type = 1
  UsePlacement = false
FEATURE [PartDesign::Body] Body140
  Group = -> [Sketch249,Pad044,Sketch248,Pocket136,Sketch250,Boolean045]
  Origin = -> Origin118
  Tip = -> Boolean045
COMPONENT P24 — recipe-attached ("pillar3", modeled in this document).
Construction recipe (the document's own serialized feature program — sketch geometry with constraints, then the solid features built on it; lengths are millimeters unless a unit is written):

FEATURE [PartDesign::SubShapeBinder] Binder141
  BindCopyOnChange = 0
  BindMode = 0
  ClaimChildren = true
  Fuse = false
  MakeFace = true
  OffsetFill = false
  OffsetIntersection = false
  OffsetJoinType = 0
  OffsetOpenResult = false
  PartialLoad = false
  Relative = false
  Support = -> [Sketch008]
  _Version = 2
  expr: Support = <<pillar_base_sketch>>._self
FEATURE [PartDesign::FeaturePython] BaseBend052  label="pillar3_BaseBend"  # WARN: FeaturePython — macro-defined, semantics opaque (R4)
  BendSide = 1
  BendSketch = -> Binder141
  MidPlane = false
  Reverse = false
  Suppressed = false
  length = 1684
  radius = 2
  thickness = 2
FEATURE [Sketcher::SketchObject] Sketch253
  AttachmentSupport = -> [YZ_Plane121]
  ExternalGeometry = -> [Binder141]
  FullyConstrained = true
  MapMode = 5
  Placement = pos=(0,0,0) rot=(0.57735,0.57735,0.57735;2.0944rad)
  sketch-geometry (3):
    g0: LineSegment StartX=14 StartY=0 StartZ=0 EndX=19 EndY=0 EndZ=0
    g1: LineSegment StartX=19 StartY=0 StartZ=0 EndX=19 EndY=5 EndZ=0
    g2: ArcOfCircle CenterX=14 CenterY=5 CenterZ=0 NormalX=0 NormalY=0 NormalZ=1 AngleXU=0 Radius=5 StartAngle=4.71239 EndAngle=6.28319
  constraints (7):
    c: PointOnObject(g0,g-3)
    c: Coincident(g0,g-3)
    c: Coincident(g1,g0)
    c: Vertical(g1)
    c: Tangent(g2,g1) = -1.5708
    c: Tangent(g2,g0) = -1.5708
    c: Radius(g2) = 5
FEATURE [PartDesign::Pocket] Pocket137
  BaseFeature = -> BaseBend052
  Direction = (-1,0,0)
  Length = 5
  Length2 = 5
  Midplane = true
  Profile = -> Sketch253
  ReferenceAxis = -> Sketch253 [N_Axis]
  Suppressed = false
  Type = 1
FEATURE [PartDesign::CoordinateSystem] Local_CS006  label="pillar3_base"
  AttacherType = Attacher::AttachEngine3D
  AttachmentSupport = -> [XY_Plane121]
  MapMode = 5
FEATURE [PartDesign::CoordinateSystem] Local_CS007  label="pillar3_hat_fix_Local_CS"
  AttacherType = Attacher::AttachEngine3D
  AttachmentOffset = pos=(0,2,1594) rot=(0,0,1;0rad)
  AttachmentSupport = -> [XY_Plane121]
  MapMode = 5
  Placement = pos=(0,2,1594) rot=(0,0,1;0rad)
  expr: AttachmentOffset = <<pillar3_hat_fix_placement>>.Placement
FEATURE [PartDesign::Plane] DatumPlane007
  AttachmentOffset = pos=(0,0,842) rot=(0,0,1;0rad)
  AttachmentSupport = -> [XY_Plane121]
  Length = 60
  MapMode = 5
  Placement = pos=(0,0,842) rot=(0,0,1;0rad)
  ResizeMode = 0
  Width = 60
  expr: .AttachmentOffset.Base.z = <<pillar3_BaseBend>>.length / 2
FEATURE [PartDesign::Mirrored] Mirrored020
  BaseFeature = -> Pocket137
  MirrorPlane = -> DatumPlane007
  Originals = -> [Pocket137]
  Suppressed = false
FEATURE [PartDesign::CoordinateSystem] Local_CS009  label="pillar3_dec_corner_LCS"
  AttacherType = Attacher::AttachEngine3D
  AttachmentOffset = pos=(0,0,470) rot=(0,0,1;0rad)
  AttachmentSupport = -> [XY_Plane121]
  MapMode = 5
  Placement = pos=(0,0,470) rot=(0,0,1;0rad)
  expr: AttachmentOffset = <<pillar3_dec_corner_placement>>.Placement
FEATURE [Sketcher::SketchObject] Sketch268
  AttachmentSupport = -> [YZ_Plane121]
  FullyConstrained = false
  MapMode = 5
  Placement = pos=(0,0,0) rot=(0.57735,0.57735,0.57735;2.0944rad)
  sketch-geometry (7):
    g0: Circle CenterX=11.5 CenterY=9 CenterZ=0 NormalX=0 NormalY=0 NormalZ=1 AngleXU=0 Radius=1.7
    g1: Circle CenterX=11.5 CenterY=40.3333 CenterZ=0 NormalX=0 NormalY=0 NormalZ=1 AngleXU=0 Radius=1.7
    g2: Circle CenterX=11.5 CenterY=71.6667 CenterZ=0 NormalX=0 NormalY=0 NormalZ=1 AngleXU=0 Radius=1.7
    g3: LineSegment StartX=11.5 StartY=9 StartZ=0 EndX=11.5 EndY=40.3333 EndZ=0
    g4: LineSegment StartX=11.5 StartY=40.3333 StartZ=0 EndX=11.5 EndY=71.6667 EndZ=0
    g5: Circle CenterX=11.5 CenterY=103 CenterZ=0 NormalX=0 NormalY=0 NormalZ=1 AngleXU=0 Radius=1.86607
    g6: LineSegment StartX=11.5 StartY=103 StartZ=0 EndX=11.5 EndY=71.6667 EndZ=0
  constraints (17):
    c: Equal(g0,g1)
    c: Equal(g0,g2)
    c: Diameter(g0) = 3.4
    c: Coincident(g3,g0)
    c: Coincident(g3,g1)
    c: Coincident(g3,g4)
    c: Coincident(g4,g2)
    c: Vertical(g4)
    c: Vertical(g3)
    c: Equal(g3,g4)
    c: Coincident(g6,g5)
    c: Coincident(g6,g2)
    c: Vertical(g6)
    c: DistanceY(g0) = 9
    c: DistanceX(g0) = 11.5
    c: Equal(g6,g4)
    c: DistanceY(g5) = 103
FEATURE [PartDesign::CoordinateSystem] Local_CS047  label="pillar3_bottom_LCS"
  AttacherType = Attacher::AttachEngine3D
  AttachmentOffset = pos=(18.3,4,0) rot=(0,0,1;1.5708rad)
  AttachmentSupport = -> [XY_Plane121]
  MapMode = 5
  Placement = pos=(18.3,4,0) rot=(0,0,1;1.5708rad)
FEATURE [PartDesign::Boolean] Boolean049
  BaseFeature = -> Mirrored020
  Group = -> [Compound099]
  Suppressed = false
  Type = 1
  UsePlacement = true
FEATURE [PartDesign::Pocket] Pocket144
  BaseFeature = -> Boolean049
  Direction = (-1,0,0)
  Length = 5
  Length2 = 5
  Midplane = true
  Profile = -> Sketch268
  ReferenceAxis = -> Sketch268 [N_Axis]
  Suppressed = false
  Type = 1
FEATURE [PartDesign::Body] Body141  label="pillar3"
  Group = -> [Binder141,BaseBend052,Sketch253,Pocket137,Local_CS006,Local_CS007,DatumPlane007,Mirrored020,Local_CS009,Boolean049,Sketch268,Local_CS047,Pocket144]
  Origin = -> Origin122
  Tip = -> Pocket144
COMPONENT P25 — recipe-attached ("hat3_base", modeled in this document).
Construction recipe (the document's own serialized feature program — sketch geometry with constraints, then the solid features built on it; lengths are millimeters unless a unit is written):

FEATURE [PartDesign::SubShapeBinder] Binder142
  BindCopyOnChange = 0
  BindMode = 0
  ClaimChildren = true
  Context = -> Body142 [Binder142.]
  Fuse = false
  MakeFace = true
  OffsetFill = false
  OffsetIntersection = false
  OffsetJoinType = 0
  OffsetOpenResult = false
  PartialLoad = false
  Relative = true
  Support = -> [Connect005]
  _Version = 2
FEATURE [PartDesign::Pad] Pad045
  Direction = (0,0,1)
  Length = 3
  Length2 = 10
  Profile = -> Binder142
  Refine = true
  Suppressed = false
  Type = 0
FEATURE [PartDesign::CoordinateSystem] Local_CS037  label="hat3_bottom_bottom_LCS"
  AttacherType = Attacher::AttachEngine3D
  AttachmentSupport = -> [XY_Plane122]
  MapMode = 2
FEATURE [PartDesign::CoordinateSystem] Local_CS038  label="hat3_bottom_top_LCS"
  AttacherType = Attacher::AttachEngine3D
  AttachmentOffset = pos=(0,0,3) rot=(0,0,1;0rad)
  AttachmentSupport = -> [XY_Plane122]
  MapMode = 5
  Placement = pos=(0,0,3) rot=(0,0,1;0rad)
FEATURE [PartDesign::Boolean] Boolean050
  BaseFeature = -> Pad045
  Group = -> [Compound102]
  Suppressed = false
  Type = 1
  UsePlacement = true
FEATURE [PartDesign::Body] Body142  label="hat3_base"
  Group = -> [Binder142,Pad045,Boolean050,Local_CS037,Local_CS038]
  Origin = -> Origin123
  Tip = -> Boolean050
COMPONENT P26 — recipe-attached ("hat3_cap", modeled in this document).
Construction recipe (the document's own serialized feature program — sketch geometry with constraints, then the solid features built on it; lengths are millimeters unless a unit is written):

FEATURE [PartDesign::SubShapeBinder] Binder146
  BindCopyOnChange = 0
  BindMode = 0
  ClaimChildren = true
  Context = -> Body143 [Binder146.]
  Fuse = false
  MakeFace = true
  OffsetFill = false
  OffsetIntersection = false
  OffsetJoinType = 0
  OffsetOpenResult = false
  PartialLoad = false
  Relative = false
  Support = -> [Connect007]
  _Version = 2
FEATURE [PartDesign::Pad] Pad046
  Direction = (0,0,1)
  Length = 3
  Length2 = 10
  Profile = -> Binder146
  Refine = true
  Suppressed = false
  Type = 0
FEATURE [PartDesign::CoordinateSystem] Local_CS044  label="hat3_cap_bottom_LCS"
  AttacherType = Attacher::AttachEngine3D
  AttachmentSupport = -> [XY_Plane123]
  MapMode = 5
FEATURE [PartDesign::CoordinateSystem] Local_CS045  label="hat3_cap_top_LCS"
  AttacherType = Attacher::AttachEngine3D
  AttachmentOffset = pos=(0,0,3) rot=(0,0,1;0rad)
  AttachmentSupport = -> [XY_Plane123]
  MapMode = 5
  Placement = pos=(0,0,3) rot=(0,0,1;0rad)
FEATURE [PartDesign::Body] Body143  label="hat3_cap"
  Group = -> [Binder146,Pad046,Local_CS044,Local_CS045]
  Origin = -> Origin124
  Tip = -> Pad046
COMPONENT P27 — recipe-attached ("pillar3_hat_fix", modeled in this document).
Construction recipe (the document's own serialized feature program — sketch geometry with constraints, then the solid features built on it; lengths are millimeters unless a unit is written):

FEATURE [PartDesign::SubShapeBinder] Binder143
  BindCopyOnChange = 0
  BindMode = 0
  ClaimChildren = true
  Fuse = false
  MakeFace = true
  OffsetFill = false
  OffsetIntersection = false
  OffsetJoinType = 0
  OffsetOpenResult = false
  PartialLoad = false
  Placement = pos=(0,0,0) rot=(0,-1,0;1.5708rad)
  Relative = false
  Support = -> [Sketch251]
  _Version = 2
FEATURE [PartDesign::FeaturePython] BaseBend053  label="pillar3_hat_fix_BaseBend"  # WARN: FeaturePython — macro-defined, semantics opaque (R4)
  BendSide = 1
  BendSketch = -> Binder143
  MidPlane = true
  Reverse = false
  Suppressed = false
  length = 28.6
  radius = 2
  thickness = 1.5
  expr: length = <<pillar_base_sketch>>.Constraints.width - 8 mm
FEATURE [Sketcher::SketchObject] Sketch256
  AttachmentSupport = -> [XY_Plane124]
  ExternalGeometry = -> [Binder143]
  FullyConstrained = true
  MapMode = 5
  expr: Constraints[12] = <<pillar3_hat_fix_BaseBend>>.length
  sketch-geometry (6):
    g0: LineSegment StartX=9.3 StartY=70 StartZ=0 EndX=14.3 EndY=70 EndZ=0
    g1: LineSegment StartX=14.3 StartY=70 StartZ=0 EndX=14.3 EndY=65 EndZ=0
    g2: LineSegment StartX=-14.3 StartY=65 StartZ=0 EndX=-14.3 EndY=70 EndZ=0
    g3: LineSegment StartX=-14.3 StartY=70 StartZ=0 EndX=-9.3 EndY=70 EndZ=0
    g4: ArcOfCircle CenterX=9.3 CenterY=65 CenterZ=0 NormalX=0 NormalY=0 NormalZ=1 AngleXU=0 Radius=5 StartAngle=4e-16 EndAngle=1.5708
    g5: ArcOfCircle CenterX=-9.3 CenterY=65 CenterZ=0 NormalX=0 NormalY=0 NormalZ=1 AngleXU=0 Radius=5 StartAngle=1.5708 EndAngle=3.14159
  constraints (15):
    c: Coincident(g0,g1)
    c: Coincident(g2,g3)
    c: Tangent(g5,g2) = 1.5708
    c: Tangent(g5,g3) = 1.5708
    c: Tangent(g4,g1) = 1.5708
    c: Tangent(g4,g0) = 1.5708
    c: Equal(g4,g5)
    c: Radius(g5) = 5
    c: Parallel(g1,g-3)
    c: Perpendicular(g-3,g0)
    c: Perpendicular(g-3,g3)
    c: Parallel(g2,g-3)
    c: DistanceX(g2,g0) = 28.6
    c: Horizontal(g2,g0)
    c: Symmetric(g0,g2,g-3)
FEATURE [Sketcher::SketchObject] Sketch257
  AttachmentOffset = pos=(0,0,4) rot=(0,0,1;0rad)
  AttachmentSupport = -> [XY_Plane124]
  ExternalGeometry = -> [Binder143]
  FullyConstrained = true
  MapMode = 5
  Placement = pos=(0,0,4) rot=(0,0,1;0rad)
  expr: Constraints[13] = <<pillar3_hat_fix_BaseBend>>.length
  sketch-geometry (6):
    g0: LineSegment StartX=9.3 StartY=30 StartZ=0 EndX=14.3 EndY=30 EndZ=0
    g1: LineSegment StartX=14.3 StartY=30 StartZ=0 EndX=14.3 EndY=25 EndZ=0
    g2: LineSegment StartX=-14.3 StartY=25 StartZ=0 EndX=-14.3 EndY=30 EndZ=0
    g3: LineSegment StartX=-14.3 StartY=30 StartZ=0 EndX=-9.3 EndY=30 EndZ=0
    g4: ArcOfCircle CenterX=9.3 CenterY=25 CenterZ=0 NormalX=0 NormalY=0 NormalZ=1 AngleXU=0 Radius=5 StartAngle=3e-16 EndAngle=1.5708
    g5: ArcOfCircle CenterX=-9.3 CenterY=25 CenterZ=0 NormalX=0 NormalY=0 NormalZ=1 AngleXU=0 Radius=5 StartAngle=1.5708 EndAngle=3.14159
  constraints (15):
    c: Coincident(g0,g1)
    c: Coincident(g2,g3)
    c: Tangent(g5,g2) = 1.5708
    c: Tangent(g5,g3) = 1.5708
    c: Tangent(g4,g1) = 1.5708
    c: Tangent(g4,g0) = 1.5708
    c: Equal(g4,g5)
    c: Radius(g4) = 5
    c: Symmetric(g2,g0,g-3)
    c: Parallel(g2,g-3)
    c: Parallel(g-3,g1)
    c: Perpendicular(g0,g1)
    c: Horizontal(g0,g-3)
    c: DistanceX(g2,g0) = 28.6
    c: Perpendicular(g-3,g3)
FEATURE [PartDesign::CoordinateSystem] Local_CS005
  AttacherType = Attacher::AttachEngine3D
  AttachmentSupport = -> [XY_Plane124]
  MapMode = 5
FEATURE [Sketcher::SketchObject] Sketch265
  AttachmentSupport = -> [XY_Plane124]
  FullyConstrained = true
  MapMode = 5
  expr: Constraints[4] = <<pillar3_hat_fix_BaseBend>>.length / 2
  sketch-geometry (8):
    g0: LineSegment StartX=11.3 StartY=14 StartZ=0 EndX=10 EndY=14 EndZ=0
    g1: ArcOfCircle CenterX=10 CenterY=9 CenterZ=0 NormalX=0 NormalY=0 NormalZ=1 AngleXU=0 Radius=5 StartAngle=1.5708 EndAngle=3.14159
    g2: LineSegment StartX=5 StartY=9 StartZ=0 EndX=5 EndY=1 EndZ=0
    g3: LineSegment StartX=14.3 StartY=17 StartZ=0 EndX=14.3 EndY=-7 EndZ=0
    g4: ArcOfCircle CenterX=10 CenterY=1 CenterZ=0 NormalX=0 NormalY=0 NormalZ=1 AngleXU=0 Radius=5 StartAngle=3.14159 EndAngle=4.71239
    g5: ArcOfCircle CenterX=11.3 CenterY=-7 CenterZ=0 NormalX=0 NormalY=0 NormalZ=1 AngleXU=0 Radius=3 StartAngle=-7.46e-14 EndAngle=1.5708
    g6: ArcOfCircle CenterX=11.3 CenterY=17 CenterZ=0 NormalX=0 NormalY=0 NormalZ=1 AngleXU=0 Radius=3 StartAngle=4.71239 EndAngle=6.28319
    g7: LineSegment StartX=10 StartY=-4 StartZ=0 EndX=11.3 EndY=-4 EndZ=0
  constraints (20):
    c: Horizontal(g0)
    c: Vertical(g2)
    c: Vertical(g3)
    c: Radius(g1) = 5
    c: DistanceX(g3) = 14.3
    c: Tangent(g1,g0) = -1.5708
    c: Tangent(g2,g1) = -1.5708
    c: DistanceX(g2) = 5
    c: Tangent(g0,g6) = 1.5708
    c: Tangent(g3,g6) = 1.5708
    c: Horizontal(g7)
    c: Tangent(g3,g5) = 1.5708
    c: Tangent(g4,g2) = -1.5708
    c: Tangent(g7,g4) = -1.5708
    c: Tangent(g7,g5) = 1.5708
    c: Radius(g6) = 3
    c: Equal(g6,g5)
    c: Equal(g4,g1)
    c: DistanceY(g0) = 14
    c: DistanceY(g4) = -4
FEATURE [PartDesign::FeaturePython] SketchOnSheet  # WARN: FeaturePython — macro-defined, semantics opaque (R4)
  BaseFeature = -> BaseBend053
  Sketch = -> Sketch265
  Suppressed = false
  baseObject = -> BaseBend053 [Face22]
  kfactor = 0.5
FEATURE [PartDesign::Pocket] Pocket138
  BaseFeature = -> SketchOnSheet
  Direction = (0,0,-1)
  Length = 5
  Length2 = 5
  Profile = -> Sketch256
  ReferenceAxis = -> Sketch256 [N_Axis]
  Reversed = true
  Suppressed = false
  Type = 0
FEATURE [PartDesign::Pocket] Pocket139
  BaseFeature = -> Pocket138
  Direction = (0,0,-1)
  Length = 5
  Length2 = 5
  Profile = -> Sketch257
  ReferenceAxis = -> Sketch257 [N_Axis]
  Reversed = true
  Suppressed = false
  Type = 1
FEATURE [PartDesign::Boolean] Boolean046
  BaseFeature = -> Pocket139
  Group = -> [Compound094]
  Suppressed = false
  Type = 1
  UsePlacement = true
FEATURE [PartDesign::Body] Body144  label="pillar3_hat_fix"
  Group = -> [Binder143,BaseBend053,Sketch256,Sketch257,SketchOnSheet,Pocket138,Pocket139,Local_CS005,Boolean046,Sketch265]
  Origin = -> Origin125
  Tip = -> Boolean046
COMPONENT P28 — recipe-attached ("pilllar3_dec_corner", modeled in this document).
Construction recipe (the document's own serialized feature program — sketch geometry with constraints, then the solid features built on it; lengths are millimeters unless a unit is written):

FEATURE [PartDesign::SubShapeBinder] Binder144
  BindCopyOnChange = 0
  BindMode = 0
  ClaimChildren = true
  Context = -> Body145 [Binder144.]
  Fuse = false
  MakeFace = true
  OffsetFill = false
  OffsetIntersection = false
  OffsetJoinType = 0
  OffsetOpenResult = false
  PartialLoad = false
  Relative = true
  Support = -> [Sketch056]
  _Version = 2
  expr: Support = <<pillar_dec_corner_base_sketch>>._self
FEATURE [PartDesign::FeaturePython] BaseBend054  label="pillar3_dec_corner_BaseBend"  # WARN: FeaturePython — macro-defined, semantics opaque (R4)
  BendSide = 0
  BendSketch = -> Binder144
  MidPlane = false
  Reverse = false
  Suppressed = false
  length = 1214
  radius = 2
  thickness = 0.5
  expr: length = <<pillar3_BaseBend>>.length - <<pillar3_dec_corner_placement>>.Placement.Base.z
FEATURE [Sketcher::SketchObject] Sketch260
  AttachmentSupport = -> [XZ_Plane125]
  ExternalGeometry = -> [Binder144]
  FullyConstrained = true
  MapMode = 5
  Placement = pos=(0,0,0) rot=(1,0,0;1.5708rad)
  sketch-geometry (3):
    g0: LineSegment StartX=13.3 StartY=0 StartZ=0 EndX=18.3 EndY=-3e-16 EndZ=0
    g1: LineSegment StartX=18.3 StartY=-3e-16 StartZ=0 EndX=18.3 EndY=5 EndZ=0
    g2: ArcOfCircle CenterX=13.3 CenterY=5 CenterZ=0 NormalX=0 NormalY=0 NormalZ=1 AngleXU=0 Radius=5 StartAngle=4.71239 EndAngle=6.28319
  constraints (7):
    c: PointOnObject(g0,g-3)
    c: Coincident(g0,g-3)
    c: Coincident(g0,g1)
    c: Vertical(g1)
    c: Tangent(g2,g1) = -1.5708
    c: Tangent(g2,g0) = -1.5708
    c: Radius(g2) = 5
FEATURE [Sketcher::SketchObject] Sketch261
  AttachmentSupport = -> [YZ_Plane125]
  ExternalGeometry = -> [Binder144]
  FullyConstrained = true
  MapMode = 5
  Placement = pos=(0,0,0) rot=(0.57735,0.57735,0.57735;2.0944rad)
  sketch-geometry (3):
    g0: LineSegment StartX=14 StartY=9e-16 StartZ=0 EndX=19 EndY=0 EndZ=0
    g1: LineSegment StartX=19 StartY=0 StartZ=0 EndX=19 EndY=5 EndZ=0
    g2: ArcOfCircle CenterX=14 CenterY=5 CenterZ=0 NormalX=0 NormalY=0 NormalZ=1 AngleXU=0 Radius=5 StartAngle=4.71239 EndAngle=6.28319
  constraints (7):
    c: PointOnObject(g0,g-3)
    c: Coincident(g0,g-3)
    c: Coincident(g0,g1)
    c: Vertical(g1)
    c: Tangent(g2,g1) = -1.5708
    c: Tangent(g2,g0) = -1.5708
    c: Radius(g2) = 5
FEATURE [PartDesign::Pocket] Pocket140
  BaseFeature = -> BaseBend054
  Direction = (0,1,-2e-16)
  Length = 5
  Length2 = 5
  Midplane = true
  Profile = -> Sketch260
  ReferenceAxis = -> Sketch260 [N_Axis]
  Suppressed = false
  Type = 1
FEATURE [PartDesign::Pocket] Pocket141
  BaseFeature = -> Pocket140
  Direction = (-1,0,0)
  Length = 5
  Length2 = 5
  Midplane = true
  Profile = -> Sketch261
  ReferenceAxis = -> Sketch261 [N_Axis]
  Suppressed = false
  Type = 1
FEATURE [PartDesign::Plane] DatumPlane008
  AttachmentOffset = pos=(0,0,607) rot=(0,0,1;0rad)
  AttachmentSupport = -> [XY_Plane125]
  Length = 60
  MapMode = 5
  Placement = pos=(0,0,607) rot=(0,0,1;0rad)
  ResizeMode = 0
  Width = 60
  expr: .AttachmentOffset.Base.z = <<pillar3_dec_corner_BaseBend>>.length / 2
FEATURE [PartDesign::Mirrored] Mirrored021
  BaseFeature = -> Pocket141
  MirrorPlane = -> DatumPlane008
  Originals = -> [Pocket140,Pocket141]
  Suppressed = false
FEATURE [PartDesign::CoordinateSystem] Local_CS008  label="pilllar3_dec_corner_base_local_cs"
  AttacherType = Attacher::AttachEngine3D
  AttachmentSupport = -> [XY_Plane125]
  MapMode = 5
FEATURE [PartDesign::Boolean] Boolean048
  BaseFeature = -> Mirrored021
  Group = -> [Compound098]
  Suppressed = false
  Type = 1
  UsePlacement = true
FEATURE [PartDesign::Body] Body145  label="pilllar3_dec_corner"
  Group = -> [Binder144,BaseBend054,Sketch260,Sketch261,Pocket140,Pocket141,DatumPlane008,Mirrored021,Local_CS008,Boolean048]
  Origin = -> Origin126
  Tip = -> Boolean048
COMPONENT P29 — recipe-attached ("hat3_plexiglass", modeled in this document).
Construction recipe (the document's own serialized feature program — sketch geometry with constraints, then the solid features built on it; lengths are millimeters unless a unit is written):

FEATURE [PartDesign::SubShapeBinder] Binder145
  BindCopyOnChange = 0
  BindMode = 0
  ClaimChildren = true
  Context = -> Body146 [Binder145.]
  Fuse = false
  MakeFace = true
  OffsetFill = false
  OffsetIntersection = false
  OffsetJoinType = 0
  OffsetOpenResult = false
  PartialLoad = false
  Relative = false
  Support = -> [Connect006]
  _Version = 2
FEATURE [PartDesign::FeaturePython] BaseBend055  # WARN: FeaturePython — macro-defined, semantics opaque (R4)
  BendSide = 1
  BendSketch = -> Binder145
  MidPlane = false
  Reverse = false
  Suppressed = false
  length = 100
  radius = 1
  thickness = 1.5
FEATURE [PartDesign::FeaturePython] Extend002  # WARN: FeaturePython — macro-defined, semantics opaque (R4)
  BaseFeature = -> BaseBend055
  Offset = 0.02
  Refine = true
  Suppressed = false
  UseSubtraction = false
  baseObject = -> BaseBend055 [Face1]
  gap1 = 0
  gap2 = 0
  length = 0
FEATURE [PartDesign::Boolean] Boolean047
  BaseFeature = -> Extend002
  Group = -> [Compound096]
  Suppressed = false
  Type = 1
  UsePlacement = true
FEATURE [Sketcher::SketchObject] Sketch278
  AttachmentOffset = pos=(0,0,0) rot=(0,1,0;1.5708rad)
  AttachmentSupport = -> [Binder145]
  FullyConstrained = true
  MapMode = 7
  Placement = pos=(113.449,65.5,0) rot=(-0.774597,0.447214,0.447214;4.45971rad)
  sketch-geometry (1):
    g0: Circle CenterX=0 CenterY=22 CenterZ=0 NormalX=0 NormalY=0 NormalZ=1 AngleXU=0 Radius=1.7
  constraints (3):
    c: PointOnObject(g0,g-2)
    c: Diameter(g0) = 3.4
    c: DistanceY(g0) = 22
FEATURE [PartDesign::Pocket] Pocket146
  BaseFeature = -> Boolean047
  Direction = (0.866025,0.5,0)
  Length = 5
  Length2 = 5
  Midplane = true
  Profile = -> Sketch278
  ReferenceAxis = -> Sketch278 [N_Axis]
  Suppressed = false
  Type = 1
FEATURE [PartDesign::CoordinateSystem] Local_CS050  label="hat3_plexiglass_LCS"
  AttacherType = Attacher::AttachEngine3D
  AttachmentSupport = -> [XY_Plane126]
  MapMode = 5
FEATURE [PartDesign::Body] Body146  label="hat3_plexiglass"
  Group = -> [Binder145,BaseBend055,Extend002,Boolean047,Sketch278,Pocket146,Local_CS050]
  Origin = -> Origin127
  Tip = -> Pocket146
COMPONENT P30 — recipe-attached ("pilllar3_dec_corner_mirror", modeled in this document).
Construction recipe (the document's own serialized feature program — sketch geometry with constraints, then the solid features built on it; lengths are millimeters unless a unit is written):

FEATURE [PartDesign::SubShapeBinder] Binder148
  BindCopyOnChange = 0
  BindMode = 0
  ClaimChildren = true
  Context = -> Body147 [Binder148.]
  Fuse = false
  MakeFace = true
  OffsetFill = false
  OffsetIntersection = false
  OffsetJoinType = 0
  OffsetOpenResult = false
  PartialLoad = false
  Relative = false
  Support = -> [Part__Mirroring037]
  _Version = 2
FEATURE [PartDesign::FeaturePython] BaseBend056  label="pilllar3_dec_corner_mirror_BaseBend"  # WARN: FeaturePython — macro-defined, semantics opaque (R4)
  BendSide = 1
  BendSketch = -> Binder148
  MidPlane = false
  Reverse = false
  Suppressed = false
  length = 1214
  radius = 2
  thickness = 0.5
  expr: length = <<pillar3_dec_corner_BaseBend>>.length
  expr: radius = <<pillar3_dec_corner_BaseBend>>.radius
  expr: thickness = <<pillar3_dec_corner_BaseBend>>.thickness
FEATURE [Sketcher::SketchObject] Sketch266
  AttachmentSupport = -> [XZ_Plane127]
  ExternalGeometry = -> [Binder148]
  FullyConstrained = true
  MapMode = 5
  Placement = pos=(0,0,0) rot=(1,0,0;1.5708rad)
  sketch-geometry (3):
    g0: ArcOfCircle CenterX=-13.3 CenterY=5 CenterZ=0 NormalX=0 NormalY=0 NormalZ=1 AngleXU=0 Radius=5 StartAngle=3.14159 EndAngle=4.71239
    g1: LineSegment StartX=-18.3 StartY=5 StartZ=0 EndX=-18.3 EndY=0 EndZ=0
    g2: LineSegment StartX=-18.3 StartY=0 StartZ=0 EndX=-13.3 EndY=-3e-16 EndZ=0
  constraints (7):
    c: PointOnObject(g0,g-3)
    c: Coincident(g1,g2)
    c: Vertical(g1)
    c: Coincident(g1,g-3)
    c: Tangent(g0,g1) = -1.5708
    c: Radius(g0) = 5
    c: Tangent(g2,g0) = -1.5708
FEATURE [Sketcher::SketchObject] Sketch267
  AttachmentSupport = -> [YZ_Plane127]
  ExternalGeometry = -> [Binder148]
  FullyConstrained = true
  MapMode = 5
  Placement = pos=(0,0,0) rot=(0.57735,0.57735,0.57735;2.0944rad)
  sketch-geometry (3):
    g0: LineSegment StartX=14 StartY=6.04e-13 StartZ=0 EndX=19 EndY=0 EndZ=0
    g1: LineSegment StartX=19 StartY=0 StartZ=0 EndX=19 EndY=5 EndZ=0
    g2: ArcOfCircle CenterX=14 CenterY=5 CenterZ=0 NormalX=0 NormalY=0 NormalZ=1 AngleXU=0 Radius=5 StartAngle=4.71239 EndAngle=6.28319
  constraints (7):
    c: PointOnObject(g0,g-1)
    c: Coincident(g0,g1)
    c: Vertical(g1)
    c: Coincident(g0,g-3)
    c: Tangent(g2,g1) = -1.5708
    c: Tangent(g2,g0) = -1.5708
    c: Radius(g2) = 5
FEATURE [PartDesign::Pocket] Pocket142
  BaseFeature = -> BaseBend056
  Direction = (0,1,-2e-16)
  Length = 5
  Length2 = 5
  Midplane = true
  Profile = -> Sketch266
  ReferenceAxis = -> Sketch266 [N_Axis]
  Suppressed = false
  Type = 1
FEATURE [PartDesign::Pocket] Pocket143
  BaseFeature = -> Pocket142
  Direction = (-1,0,0)
  Length = 5
  Length2 = 5
  Midplane = true
  Profile = -> Sketch267
  ReferenceAxis = -> Sketch267 [N_Axis]
  Suppressed = false
  Type = 1
FEATURE [PartDesign::Plane] DatumPlane009
  AttachmentOffset = pos=(0,0,607) rot=(0,0,1;0rad)
  AttachmentSupport = -> [XY_Plane127]
  Length = 60
  MapMode = 5
  Placement = pos=(0,0,607) rot=(0,0,1;0rad)
  ResizeMode = 0
  Width = 60
  expr: .AttachmentOffset.Base.z = <<pilllar3_dec_corner_mirror_BaseBend>>.length / 2
FEATURE [PartDesign::Mirrored] Mirrored022
  BaseFeature = -> Pocket143
  MirrorPlane = -> DatumPlane009
  Originals = -> [Pocket142,Pocket143]
  Suppressed = false
FEATURE [PartDesign::Boolean] Boolean051
  BaseFeature = -> Mirrored022
  Group = -> [Compound103]
  Suppressed = false
  Type = 1
  UsePlacement = true
FEATURE [PartDesign::CoordinateSystem] Local_CS043
  AttacherType = Attacher::AttachEngine3D
  AttachmentSupport = -> [XY_Plane127]
  MapMode = 5
FEATURE [PartDesign::Body] Body147  label="pilllar3_dec_corner_mirror"
  Group = -> [Binder148,BaseBend056,Sketch266,Sketch267,Pocket142,Pocket143,DatumPlane009,Mirrored022,Boolean051,Local_CS043]
  Origin = -> Origin128
  Tip = -> Boolean051
COMPONENT P31 — recipe-attached ("basement_v4_bottom_amplifier", modeled in this document).
Construction recipe (the document's own serialized feature program — sketch geometry with constraints, then the solid features built on it; lengths are millimeters unless a unit is written):

FEATURE [PartDesign::SubShapeBinder] Binder150
  BindCopyOnChange = 0
  BindMode = 0
  ClaimChildren = true
  Context = -> Body148 [Binder150.]
  Fuse = false
  MakeFace = true
  OffsetFill = false
  OffsetIntersection = false
  OffsetJoinType = 0
  OffsetOpenResult = false
  PartialLoad = false
  Relative = false
  Support = -> [Connect008]
  _Version = 2
FEATURE [PartDesign::Pad] Pad047
  Direction = (0,0,1)
  Length = 18
  Length2 = 10
  Profile = -> Binder150
  Suppressed = false
  Type = 0
FEATURE [PartDesign::Boolean] Boolean053
  BaseFeature = -> Pad047
  Group = -> [Compound106]
  Suppressed = false
  Type = 1
  UsePlacement = true
FEATURE [PartDesign::Body] Body148  label="basement_v4_bottom_amplifier"
  Group = -> [Binder150,Pad047,Boolean053]
  Origin = -> Origin129
  Tip = -> Boolean053
COMPONENT P32 — recipe-attached ("basement_v4_bottom", modeled in this document).
Construction recipe (the document's own serialized feature program — sketch geometry with constraints, then the solid features built on it; lengths are millimeters unless a unit is written):

FEATURE [PartDesign::SubShapeBinder] Binder151
  BindCopyOnChange = 0
  BindMode = 0
  ClaimChildren = false
  Context = -> Body149 [Binder151.]
  Fuse = false
  MakeFace = true
  OffsetFill = false
  OffsetIntersection = false
  OffsetJoinType = 0
  OffsetOpenResult = false
  PartialLoad = false
  Relative = true
  Support = -> [Array002]
  _Version = 2
  expr: Support = <<basement_bottom_2d>>._self
FEATURE [PartDesign::Pad] Pad048
  Direction = (0,0,1)
  Length = 18
  Length2 = 10
  Profile = -> Binder151
  Suppressed = false
  Type = 0
FEATURE [PartDesign::Boolean] Boolean054
  BaseFeature = -> Pad048
  Group = -> [Compound107]
  Suppressed = false
  Type = 1
  UsePlacement = true
FEATURE [PartDesign::Body] Body149  label="basement_v4_bottom"
  Group = -> [Binder151,Pad048,Boolean054]
  Origin = -> Origin130
  Tip = -> Boolean054
COMPONENT P33 — recipe-attached ("basement_v4_top_amplifier", modeled in this document).
Construction recipe (the document's own serialized feature program — sketch geometry with constraints, then the solid features built on it; lengths are millimeters unless a unit is written):

FEATURE [PartDesign::SubShapeBinder] Binder153
  BindCopyOnChange = 0
  BindMode = 0
  ClaimChildren = true
  Context = -> Body150 [Binder153.]
  Fuse = false
  MakeFace = true
  OffsetFill = false
  OffsetIntersection = false
  OffsetJoinType = 0
  OffsetOpenResult = false
  PartialLoad = false
  Relative = false
  Support = -> [Connect009]
  _Version = 2
FEATURE [PartDesign::Pad] Pad050
  Direction = (0,0,1)
  Length = 18
  Length2 = 10
  Profile = -> Binder153
  Suppressed = false
  Type = 0
FEATURE [PartDesign::Boolean] Boolean055
  BaseFeature = -> Pad050
  Group = -> [Compound109]
  Suppressed = false
  Type = 1
  UsePlacement = true
FEATURE [PartDesign::Body] Body150  label="basement_v4_top_amplifier"
  Group = -> [Binder153,Pad050,Boolean055]
  Origin = -> Origin131
  Tip = -> Boolean055
COMPONENT P34 — recipe-attached ("basement_v4_top", modeled in this document).
Construction recipe (the document's own serialized feature program — sketch geometry with constraints, then the solid features built on it; lengths are millimeters unless a unit is written):

FEATURE [PartDesign::SubShapeBinder] Binder152
  BindCopyOnChange = 0
  BindMode = 0
  ClaimChildren = true
  Context = -> Body151 [Binder152.]
  Fuse = true
  MakeFace = false
  OffsetFill = false
  OffsetIntersection = false
  OffsetJoinType = 0
  OffsetOpenResult = false
  PartialLoad = false
  Relative = false
  Support = -> [Connect010]
  _Version = 2
  expr: Support = <<Connect010>>._self
FEATURE [PartDesign::Pad] Pad049
  Direction = (0,0,1)
  Length = 18
  Length2 = 10
  Profile = -> Binder152
  Refine = true
  Suppressed = false
  Type = 0
FEATURE [Sketcher::SketchObject] Sketch277
  AttachmentOffset = pos=(-253,0,0) rot=(0,0,1;0rad)
  AttachmentSupport = -> [YZ_Plane131]
  FullyConstrained = true
  MapMode = 5
  Placement = pos=(0,-253,0) rot=(0.57735,0.57735,0.57735;2.0944rad)
  sketch-geometry (3):
    g0: LineSegment StartX=0 StartY=15 StartZ=0 EndX=0 EndY=0 EndZ=0
    g1: LineSegment StartX=0 StartY=0 StartZ=0 EndX=15 EndY=0 EndZ=0
    g2: LineSegment StartX=15 StartY=0 StartZ=0 EndX=0 EndY=15 EndZ=0
  constraints (8):
    c: PointOnObject(g0,g-2)
    c: Coincident(g0,g-1)
    c: Coincident(g0,g1)
    c: PointOnObject(g1,g-1)
    c: Coincident(g1,g2)
    c: Coincident(g2,g0)
    c: Angle(g2) = 2.35619
    c: DistanceY(g0,g0) = 15
FEATURE [PartDesign::SubtractivePipe] SubtractivePipe001
  AuxilleryCurvelinear = true
  AuxillerySpineTangent = false
  BaseFeature = -> Pad049
  Binormal = (0,0,0)
  Mode = 0
  Profile = -> Sketch277
  Spine = -> Binder152 [Edge14,Edge13,Edge12,Edge11,Edge10,Edge9,Edge8,Edge7,Edge6,Edge5,Edge4,Edge3,Edge2,Edge1,Edge18,Edge17,Edge16,Edge15]
  SpineTangent = false
  Suppressed = false
  Transformation = 0
  Transition = 0
FEATURE [PartDesign::Boolean] Boolean056
  BaseFeature = -> SubtractivePipe001
  Group = -> [Compound110]
  Refine = true
  Suppressed = false
  Type = 1
  UsePlacement = true
FEATURE [PartDesign::Body] Body151  label="basement_v4_top"
  Group = -> [Binder152,Pad049,SubtractivePipe001,Boolean056,Sketch277]
  Origin = -> Origin132
  Tip = -> SubtractivePipe001
COMPONENT P35 — recipe-attached ("pillar3_plexiglass_outer", modeled in this document).
Construction recipe (the document's own serialized feature program — sketch geometry with constraints, then the solid features built on it; lengths are millimeters unless a unit is written):

FEATURE [PartDesign::SubShapeBinder] Binder154
  BindCopyOnChange = 0
  BindMode = 0
  ClaimChildren = true
  Context = -> Body152 [Binder154.]
  Fuse = false
  MakeFace = true
  OffsetFill = false
  OffsetIntersection = false
  OffsetJoinType = 0
  OffsetOpenResult = false
  PartialLoad = false
  Relative = true
  Support = -> [Connect012]
  _Version = 2
FEATURE [PartDesign::FeaturePython] BaseBend057  # WARN: FeaturePython — macro-defined, semantics opaque (R4)
  BendSide = 1
  BendSketch = -> Binder154
  MidPlane = false
  Reverse = false
  Suppressed = false
  length = 1214
  radius = 1
  thickness = 1.5
FEATURE [PartDesign::Boolean] Boolean057
  BaseFeature = -> BaseBend057
  Group = -> [Compound113]
  Refine = true
  Suppressed = false
  Type = 1
  UsePlacement = true
FEATURE [PartDesign::CoordinateSystem] Local_CS049
  AttacherType = Attacher::AttachEngine3D
  AttachmentSupport = -> [XY_Plane132]
  MapMode = 5
FEATURE [PartDesign::Body] Body152  label="pillar3_plexiglass_outer"
  Group = -> [Binder154,BaseBend057,Boolean057,Local_CS049]
  Origin = -> Origin133
  Tip = -> Boolean057
COMPONENT P36 — geometry summary ("leg_amplifier_link"; no construction recipe available for this part):
  bounding box: 403.5 x 29.1 x 24.5 mm
  tessellated surface: 76 triangles
  volume: 6293 mm^3 (2% of its bounding box)
  symmetry: mirror-symmetric across its z mid-plane
COMPONENT P37 — recipe-attached ("hub2108", modeled in this document).
Construction recipe (the document's own serialized feature program — sketch geometry with constraints, then the solid features built on it; lengths are millimeters unless a unit is written):

FEATURE [PartDesign::SubShapeBinder] Binder
  BindCopyOnChange = 0
  BindMode = 0
  ClaimChildren = true
  Context = -> Body [Binder.]
  Fuse = false
  MakeFace = true
  OffsetFill = false
  OffsetIntersection = false
  OffsetJoinType = 0
  OffsetOpenResult = false
  PartialLoad = false
  Relative = true
  Support = -> [Compound001]
  _Version = 2
  expr: Support = <<part1_base>>._self
FEATURE [PartDesign::FeaturePython] BaseBend  # WARN: FeaturePython — macro-defined, semantics opaque (R4)
  BendSide = 1
  BendSketch = -> Binder
  MidPlane = false
  Reverse = false
  Suppressed = false
  length = 1428
  radius = 0.1
  thickness = 0.3
  expr: length = <<Properties>>.total_height
  expr: radius = composit_properties#<<Properties>>.bend_r
  expr: thickness = composit_properties#<<Properties>>.al_thickness
FEATURE [Sketcher::SketchObject] Sketch044
  AttachmentSupport = -> [YZ_Plane]
  ExternalGeometry = -> [Binder]
  FullyConstrained = false
  MapMode = 5
  Placement = pos=(0,0,0) rot=(0.57735,0.57735,0.57735;2.0944rad)
  expr: Constraints[16] = <<Properties>>.total_height
  expr: Constraints[23] = composit_properties#<<Properties>>.bend_r
  expr: Constraints[33] = <<Properties>>.petal_offset
  sketch-geometry (12):
    g0: LineSegment StartX=-41.6284 StartY=0 StartZ=0 EndX=4.96521 EndY=0 EndZ=0
    g1: LineSegment StartX=4.96521 StartY=0 StartZ=0 EndX=4.96521 EndY=512 EndZ=0
    g2: LineSegment StartX=4.96521 StartY=512 StartZ=0 EndX=-41.6284 EndY=512 EndZ=0
    g3: LineSegment StartX=-41.6284 StartY=512 StartZ=0 EndX=-41.6284 EndY=0 EndZ=0
    g4: LineSegment StartX=-41.6284 StartY=1428 StartZ=0 EndX=8.37158 EndY=1428 EndZ=0
    g5: LineSegment StartX=4.96521 StartY=1354 StartZ=0 EndX=-41.6284 EndY=1354 EndZ=0
    g6: LineSegment StartX=-41.6284 StartY=1354 StartZ=0 EndX=-41.6284 EndY=1428 EndZ=0
    g7: ArcOfCircle CenterX=4.96521 CenterY=0.1 CenterZ=0 NormalX=0 NormalY=0 NormalZ=1 AngleXU=0 Radius=0.1 StartAngle=3.66519 EndAngle=4.71239
    g8: LineSegment StartX=4.96521 StartY=0 StartZ=0 EndX=6.6679 EndY=0 EndZ=0
    g9: LineSegment StartX=4.87861 StartY=0.05 StartZ=0 EndX=2.02073 EndY=5 EndZ=0
    g10: LineSegment StartX=8.37158 StartY=1428 StartZ=0 EndX=4.96521 EndY=1424.59 EndZ=0
    g11: LineSegment StartX=4.96521 StartY=1424.59 StartZ=0 EndX=4.96521 EndY=1354 EndZ=0
  constraints (35):
    c: Coincident(g0,g1)
    c: Coincident(g1,g2)
    c: Coincident(g2,g3)
    c: Coincident(g3,g0)
    c: Horizontal(g0)
    c: Horizontal(g2)
    c: Vertical(g1)
    c: Vertical(g3)
    c: PointOnObject(g0,g-1)
    c: Coincident(g4,g10)
    c: Coincident(g11,g5)
    c: Coincident(g5,g6)
    c: Coincident(g6,g4)
    c: Horizontal(g4)
    c: Horizontal(g5)
    c: Vertical(g6)
    c: DistanceY(g4) = 1428
    c: DistanceY(g11,g10) = 74
    c: PointOnObject(g7,g-1)
    c: PointOnObject(g8,g-1)
    c: Tangent(g8,g7) = -1.5708
    c: Tangent(g9,g7) = 1.5708
    c: Angle(g9) = 2.0944
    c: Radius(g7) = 0.1
    c: PointOnObject(g-3,g9)
    c: DistanceY(g9) = 5
    c: PointOnObject(g7,g1)
    c: DistanceY(g1,g11) = 842
    c: Vertical(g2,g5)
    c: DistanceX(g4,g4) = 50
    c: Coincident(g10,g11)
    c: Vertical(g11)
    c: Angle(g10) = -2.35619
    c: DistanceX(g4) = 8.37158
    c: Vertical(g5,g1)
FEATURE [PartDesign::CoordinateSystem] Local_CS025  label="part1_bottom_LCS"
  AttacherType = Attacher::AttachEngine3D
  AttachmentSupport = -> [XY_Plane]
  MapMode = 5
FEATURE [PartDesign::CoordinateSystem] Local_CS026  label="part1_top_LCS"
  AttacherType = Attacher::AttachEngine3D
  AttachmentOffset = pos=(0,0,1428) rot=(0,0,1;0rad)
  AttachmentSupport = -> [XY_Plane]
  MapMode = 5
  Placement = pos=(0,0,1428) rot=(0,0,1;0rad)
  expr: .AttachmentOffset.Base.z = <<Properties>>.total_height
FEATURE [PartDesign::Boolean] Boolean001
  BaseFeature = -> BaseBend
  Group = -> [Compound016]
  Suppressed = false
  Type = 1
  UsePlacement = false
  expr: Group = <<part1_cut1>>._self
FEATURE [PartDesign::Boolean] Boolean002
  BaseFeature = -> Boolean001
  Group = -> [Compound026]
  Refine = true
  Suppressed = false
  Type = 0
  UsePlacement = false
  expr: Group = <<part1_fuse1>>._self
FEATURE [PartDesign::Pocket] Pocket025
  BaseFeature = -> Boolean002
  Direction = (-1,0,0)
  Length = 5
  Length2 = 5
  Midplane = true
  Profile = -> Sketch044
  ReferenceAxis = -> Sketch044 [N_Axis]
  Suppressed = false
  Type = 1
FEATURE [PartDesign::Boolean] Boolean005
  BaseFeature = -> Pocket025
  Group = -> [Compound024]
  Suppressed = false
  Type = 1
  UsePlacement = false
  expr: Group = <<part1_cut2>>._self
FEATURE [PartDesign::Body] Body  label="part1_material_0.30ansi"
  Group = -> [Binder,BaseBend,Boolean001,Boolean002,Sketch044,Pocket025,Boolean005,Local_CS025,Local_CS026]
  Origin = -> Origin
  Tip = -> Boolean005
COMPONENT P38 — same part as P37; its construction recipe is shown at P37.
COMPONENT P39 — same part as P37; its construction recipe is shown at P37.
COMPONENT P40 — recipe-attached ("top_top001", modeled in this document).
Construction recipe (the document's own serialized feature program — sketch geometry with constraints, then the solid features built on it; lengths are millimeters unless a unit is written):

FEATURE [Part::FeaturePython] Connect001  label="top_top_cut1_refined"  # WARN: FeaturePython — macro-defined, semantics opaque (R4)
  Objects = -> [Compound049]
  Refine = true
  Tolerance = 0
FEATURE [PartDesign::FeatureBase] BaseFeature
  BaseFeature = -> Hole003
  Suppressed = false
  expr: BaseFeature = <<Hole003>>._self
FEATURE [PartDesign::FeatureSubtractivePython] PDW_Sub  # link proxy (typed FeaturePython)
  BaseFeature = -> BaseFeature
  Body = Body110
  ClaimChildren = true
  EditPlacementAdjustments = false
  Enabled = 1
  LinkedObject = -> Connect001
  MeshTolerance = 0.1
  PatternBase = -> Connect001
  PatternBaseOffset = 0
  PatternBaseScale = 1
  PatternBaseScaleXYZ = (1,1,1)
  PatternOffsetCut = false
  PatternOffsetIntersection = false
  PatternOffsetJoin = 0
  PatternOffsetMode = 0
  PatternOffsetSelfIntersection = false
  PatternOperation = 0
  PatternOperationDefault = None
  PatternScaleCut = false
  PatternShapeOffset = 0
  PatternShapeScale = 1
  PatternShapeScaleXYZ = (1,1,1)
  PatternToolOffset = 0
  PatternToolScale = 1
  PatternToolScaleXYZ = (1,1,1)
  RefineMesh = true
  ShapeManagement = 0
  ShowMeshProps = false
  ShowOffsetProps = false
  ShowScaleProps = false
  ShowWarnings = true
  Suppressed = false
  TipBase = -> BaseFeature
  TipBaseOffset = 0
  TipBaseScale = 1
  TipBaseScaleXYZ = (1,1,1)
  TipOffsetCut = false
  TipOffsetIntersection = false
  TipOffsetJoin = 0
  TipOffsetMode = 0
  TipOffsetSelfIntersection = false
  TipOperation = 1
  TipOperationDefault = Cut
  TipScaleCut = false
  TipShapeOffset = 0
  TipShapeScale = 1
  TipShapeScaleXYZ = (1,1,1)
  TipTool = -> Connect001
  TipToolOffset = 0
  TipToolScale = 1
  TipToolScaleXYZ = (1,1,1)
  Type = Subtractive
  UsePatternBaseAddSubShape = false
  UsePatternToolAddSubShape = false
  UseTipBaseAddSubShape = false
  UseTipToolAddSubShape = false
  Version = 0.2023.08.13
FEATURE [PartDesign::Boolean] Boolean034
  BaseFeature = -> PDW_Sub
  Group = -> [Compound082]
  Suppressed = false
  Type = 1
  UsePlacement = false
FEATURE [PartDesign::CoordinateSystem] Local_CS031  label="dropper_fix_top_outer_LCS"
  AttacherType = Attacher::AttachEngine3D
  AttachmentSupport = -> [XY_Plane083]
  MapMode = 5
FEATURE [PartDesign::CoordinateSystem] Local_CS032  label="dropper_fix_top_inner_LCS"
  AttacherType = Attacher::AttachEngine3D
  AttachmentOffset = pos=(0,0,3) rot=(0,0,1;0rad)
  AttachmentSupport = -> [XY_Plane083]
  MapMode = 5
  Placement = pos=(0,0,3) rot=(0,0,1;0rad)
FEATURE [PartDesign::Body] Body110  label="dropper_fix_top"
  Group = -> [BaseFeature,PDW_Sub,Connect001,Boolean034,Local_CS031,Local_CS032]
  Origin = -> Origin083
  Tip = -> Boolean034
